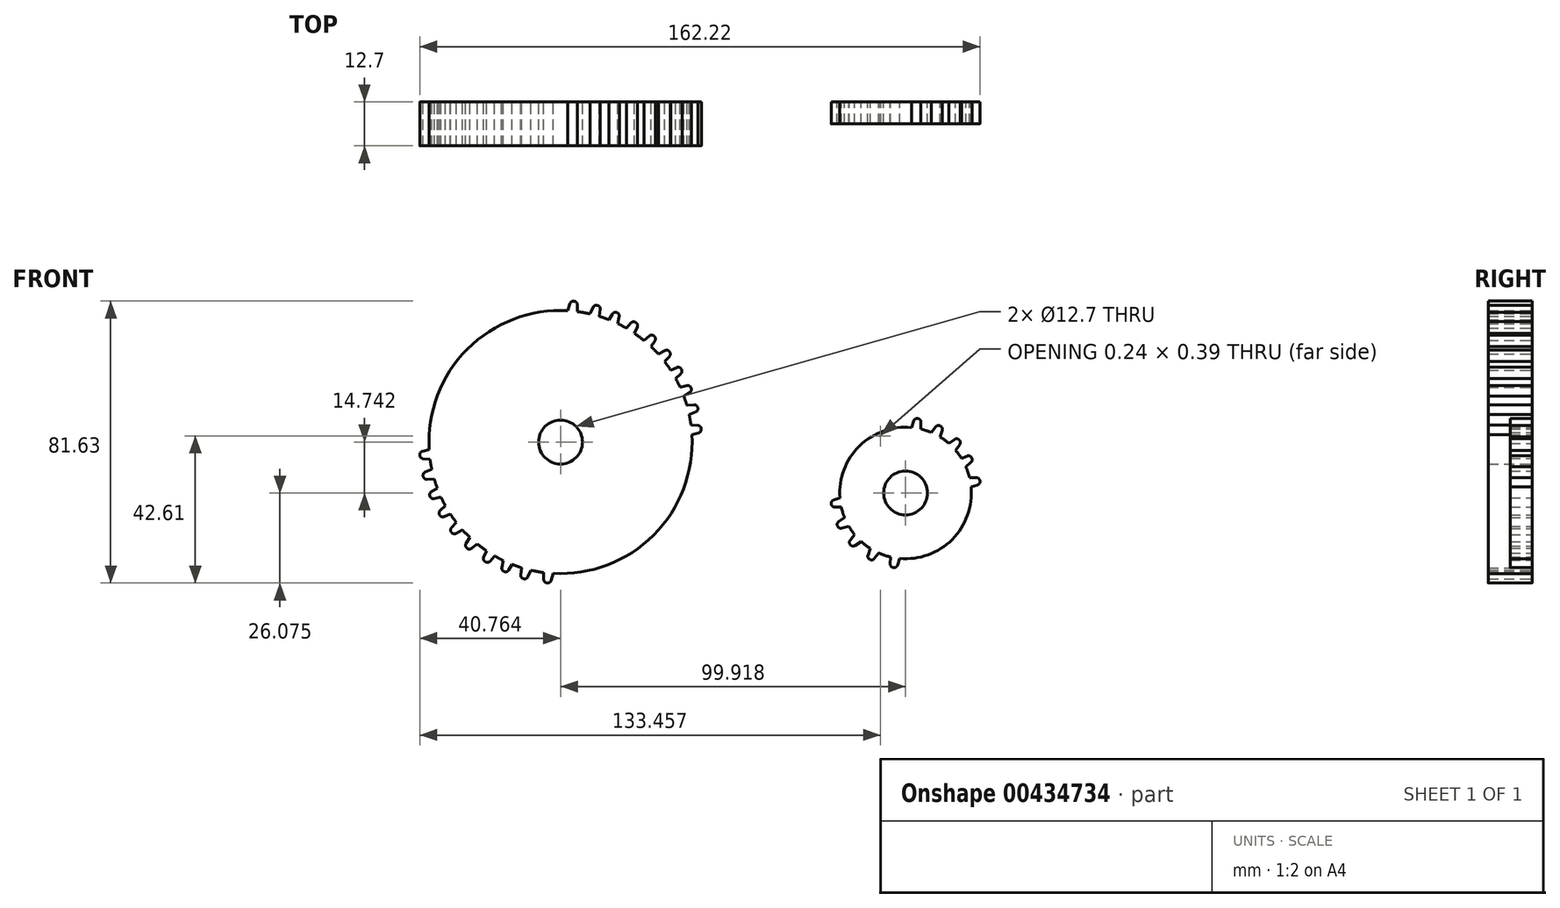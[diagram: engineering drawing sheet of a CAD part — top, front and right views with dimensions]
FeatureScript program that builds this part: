
annotation { "Feature Type Name" : "Feature", "Feature Type Description" : "" }
export const myFeature = defineFeature(function(context is Context, id is Id, definition is map)
    precondition{}
    {
        {
            var Q0;
            Q0=qCreatedBy(makeId("Front.planeOp"),FACE);
            var sketch = newSketch(context, id + "F0", { "sketchPlane" : qUnion([Q0])});
            skCircle(sketch, "E0", {"center": v(-101.86, 31.62) * mm, "radius": 38.1 * mm});
            skCircle(sketch, "E1", {"center": v(-1.94, 16.87) * mm, "radius": 19.05 * mm});
            skCircle(sketch, "E2", {"center": v(-101.86, 31.62) * mm, "radius": 6.35 * mm});
            skCircle(sketch, "E3", {"center": v(-1.94, 16.87) * mm, "radius": 6.35 * mm});
            skCircle(sketch, "E4", {"center": v(-101.86, 31.62) * mm, "radius": 36.92 * mm});
            skCircle(sketch, "E5", {"center": v(-1.94, 16.87) * mm, "radius": 17.88 * mm});
            skPoint(sketch, "E6.visualSharp", {"position": v(-61.92, 41.65) * mm});
            skLineSegment(sketch, "E7", {"start": v(-19.9, 16.87) * mm, "end": v(15.94, 16.87) * mm, "construction": true});
            skLineSegment(sketch, "E8", {"start": v(19.58, 20.42) * mm, "end": v(19.6, 20.3) * mm});
            skLineSegment(sketch, "E9", {"start": v(18.89, 19.18) * mm, "end": v(16.46, 18.44) * mm});
            skLineSegment(sketch, "E10", {"start": v(18.6, 21.3) * mm, "end": v(16.05, 21.36) * mm});
            skLineSegment(sketch, "E11", {"start": v(15.54, 20.78) * mm, "end": v(15.8, 18.85) * mm});
            skPoint(sketch, "E12.visualSharp", {"position": v(19.71, 19.44) * mm});
            skArc(sketch, "E12.filletArc", {"start": v(18.89, 19.18) * mm, "mid": v(19.44, 19.6) * mm, "end": v(19.6, 20.3) * mm});
            skPoint(sketch, "E13.visualSharp", {"position": v(19.46, 21.27) * mm});
            skArc(sketch, "E13.filletArc", {"start": v(19.58, 20.42) * mm, "mid": v(19.25, 21.04) * mm, "end": v(18.6, 21.3) * mm});
            skPoint(sketch, "E14.visualSharp", {"position": v(15.89, 18.26) * mm});
            skArc(sketch, "E14.filletArc", {"start": v(15.8, 18.85) * mm, "mid": v(16.04, 18.5) * mm, "end": v(16.46, 18.44) * mm});
            skPoint(sketch, "E15.visualSharp", {"position": v(14.72, 23.21) * mm});
            skArc(sketch, "E15.filletArc", {"start": v(16.05, 21.36) * mm, "mid": v(15.66, 21.19) * mm, "end": v(15.54, 20.78) * mm});
            skLineSegment(sketch, "E16.0", {"start": v(15.46, 21.37) * mm, "end": v(15.89, 18.26) * mm, "construction": true});
            skLineSegment(sketch, "E17", {"start": v(-1.94, 34.75) * mm, "end": v(-1.94, -1) * mm, "construction": true});
            skLineSegment(sketch, "E18", {"start": v(1.56, 38.42) * mm, "end": v(1.69, 38.4) * mm});
            skLineSegment(sketch, "E19", {"start": v(2.53, 37.38) * mm, "end": v(2.48, 34.75) * mm});
            skLineSegment(sketch, "E20", {"start": v(0.43, 37.76) * mm, "end": v(-0.44, 35.27) * mm});
            skLineSegment(sketch, "E21", {"start": v(0.22, 34.56) * mm, "end": v(2.13, 34.14) * mm});
            skPoint(sketch, "E22.visualSharp", {"position": v(2.55, 38.25) * mm});
            skArc(sketch, "E22.filletArc", {"start": v(2.53, 37.38) * mm, "mid": v(2.3, 38.05) * mm, "end": v(1.69, 38.4) * mm});
            skPoint(sketch, "E23.visualSharp", {"position": v(0.71, 38.57) * mm});
            skArc(sketch, "E23.filletArc", {"start": v(1.56, 38.42) * mm, "mid": v(0.87, 38.3) * mm, "end": v(0.43, 37.76) * mm});
            skPoint(sketch, "E24.visualSharp", {"position": v(2.47, 34.16) * mm});
            skArc(sketch, "E24.filletArc", {"start": v(1.89, 34.26) * mm, "mid": v(2.3, 34.37) * mm, "end": v(2.48, 34.75) * mm});
            skPoint(sketch, "E25.visualSharp", {"position": v(-0.37, 34.68) * mm});
            skArc(sketch, "E25.filletArc", {"start": v(-0.44, 35.27) * mm, "mid": v(-0.4, 34.85) * mm, "end": v(-0.04, 34.6) * mm});
            skLineSegment(sketch, "E26.0", {"start": v(-0.63, 34.7) * mm, "end": v(2.47, 34.16) * mm, "construction": true});
            skLineSegment(sketch, "E27", {"start": v(8.06, 36.3) * mm, "end": v(8.18, 36.25) * mm});
            skLineSegment(sketch, "E28", {"start": v(8.68, 35.03) * mm, "end": v(7.86, 32.53) * mm});
            skLineSegment(sketch, "E29", {"start": v(6.78, 36) * mm, "end": v(5.21, 33.9) * mm});
            skLineSegment(sketch, "E30", {"start": v(5.39, 33.14) * mm, "end": v(7.14, 32.23) * mm});
            skPoint(sketch, "E31.visualSharp", {"position": v(8.94, 35.85) * mm});
            skArc(sketch, "E31.filletArc", {"start": v(8.68, 35.03) * mm, "mid": v(8.65, 35.73) * mm, "end": v(8.18, 36.25) * mm});
            skPoint(sketch, "E32.visualSharp", {"position": v(7.3, 36.7) * mm});
            skArc(sketch, "E32.filletArc", {"start": v(8.06, 36.3) * mm, "mid": v(7.37, 36.4) * mm, "end": v(6.78, 36) * mm});
            skPoint(sketch, "E33.visualSharp", {"position": v(7.67, 31.96) * mm});
            skArc(sketch, "E33.filletArc", {"start": v(7.14, 32.23) * mm, "mid": v(7.57, 32.21) * mm, "end": v(7.86, 32.53) * mm});
            skPoint(sketch, "E34.visualSharp", {"position": v(4.86, 33.41) * mm});
            skArc(sketch, "E34.filletArc", {"start": v(5.21, 33.9) * mm, "mid": v(5.12, 33.48) * mm, "end": v(5.39, 33.14) * mm});
            skLineSegment(sketch, "E35", {"start": v(13.54, 32.27) * mm, "end": v(13.63, 32.18) * mm});
            skLineSegment(sketch, "E36", {"start": v(13.74, 30.87) * mm, "end": v(12.2, 28.73) * mm});
            skLineSegment(sketch, "E37", {"start": v(12.23, 32.38) * mm, "end": v(10.1, 30.84) * mm});
            skLineSegment(sketch, "E38", {"start": v(10.04, 30.07) * mm, "end": v(11.43, 28.67) * mm});
            skPoint(sketch, "E39.visualSharp", {"position": v(14.25, 31.57) * mm});
            skArc(sketch, "E39.filletArc", {"start": v(13.74, 30.87) * mm, "mid": v(13.93, 31.55) * mm, "end": v(13.63, 32.18) * mm});
            skPoint(sketch, "E40.visualSharp", {"position": v(12.93, 32.88) * mm});
            skArc(sketch, "E40.filletArc", {"start": v(13.54, 32.27) * mm, "mid": v(12.9, 32.57) * mm, "end": v(12.23, 32.38) * mm});
            skPoint(sketch, "E41.visualSharp", {"position": v(11.86, 28.25) * mm});
            skArc(sketch, "E41.filletArc", {"start": v(11.43, 28.67) * mm, "mid": v(11.83, 28.52) * mm, "end": v(12.2, 28.73) * mm});
            skPoint(sketch, "E42.visualSharp", {"position": v(9.61, 30.49) * mm});
            skArc(sketch, "E42.filletArc", {"start": v(10.1, 30.84) * mm, "mid": v(9.89, 30.47) * mm, "end": v(10.04, 30.07) * mm});
            skLineSegment(sketch, "E43.0", {"start": v(9.61, 30.49) * mm, "end": v(11.86, 28.25) * mm, "construction": true});
            skLineSegment(sketch, "E44", {"start": v(17.15, 27.13) * mm, "end": v(17.21, 27.02) * mm});
            skLineSegment(sketch, "E45", {"start": v(16.98, 25.73) * mm, "end": v(14.96, 24.05) * mm});
            skLineSegment(sketch, "E46", {"start": v(15.9, 27.57) * mm, "end": v(13.45, 26.62) * mm});
            skLineSegment(sketch, "E47", {"start": v(13.2, 25.89) * mm, "end": v(14.2, 24.18) * mm});
            skPoint(sketch, "E48.visualSharp", {"position": v(17.65, 26.28) * mm});
            skArc(sketch, "E48.filletArc", {"start": v(16.98, 25.73) * mm, "mid": v(17.34, 26.33) * mm, "end": v(17.21, 27.02) * mm});
            skPoint(sketch, "E49.visualSharp", {"position": v(16.71, 27.88) * mm});
            skArc(sketch, "E49.filletArc", {"start": v(17.15, 27.13) * mm, "mid": v(16.6, 27.58) * mm, "end": v(15.9, 27.57) * mm});
            skPoint(sketch, "E50.visualSharp", {"position": v(15.3, 21.85) * mm});
            skArc(sketch, "E50.filletArc", {"start": v(14.2, 24.18) * mm, "mid": v(14.54, 23.94) * mm, "end": v(14.96, 24.05) * mm});
            skPoint(sketch, "E51.visualSharp", {"position": v(11.92, 28.33) * mm});
            skArc(sketch, "E51.filletArc", {"start": v(13.45, 26.62) * mm, "mid": v(13.15, 26.31) * mm, "end": v(13.2, 25.89) * mm});
            skLineSegment(sketch, "E52.0", {"start": v(13.92, 25.13) * mm, "end": v(15.15, 22.2) * mm, "construction": true});
            skCircle(sketch, "E53.MirrorC", {"center": v(-1.94, 16.87) * mm, "radius": 17.88 * mm, "construction": true});
            skPoint(sketch, "E54.MirrorP", {"position": v(-6.83, 38.1) * mm});
            skArc(sketch, "E55.MirrorCS", {"start": v(-6.78, 37.23) * mm, "mid": v(-6.58, 37.9) * mm, "end": v(-5.98, 38.28) * mm});
            skArc(sketch, "E56.MirrorCS", {"start": v(-5.86, 38.3) * mm, "mid": v(-5.17, 38.21) * mm, "end": v(-4.7, 37.69) * mm});
            skLineSegment(sketch, "E57.MirrorCS", {"start": v(-4.7, 37.69) * mm, "end": v(-3.58, 34.86) * mm});
            skLineSegment(sketch, "E58.MirrorCS", {"start": v(-6.78, 37.23) * mm, "end": v(-6.63, 34.6) * mm});
            skArc(sketch, "E59.MirrorCS", {"start": v(-6.01, 34.14) * mm, "mid": v(-6.43, 34.23) * mm, "end": v(-6.63, 34.6) * mm});
            skArc(sketch, "E60.MirrorCS", {"start": v(-3.73, 35.24) * mm, "mid": v(-3.76, 34.81) * mm, "end": v(-4.1, 34.56) * mm});
            skLineSegment(sketch, "E61.MirrorCS", {"start": v(-3.51, 34.68) * mm, "end": v(-6.6, 34.01) * mm, "construction": true});
            skLineSegment(sketch, "E62.MirrorCS", {"start": v(-10.85, 35.72) * mm, "end": v(-9.04, 33.27) * mm});
            skArc(sketch, "E63.MirrorCS", {"start": v(-12.13, 36.02) * mm, "mid": v(-11.44, 36.1) * mm, "end": v(-10.85, 35.72) * mm});
            skArc(sketch, "E64.MirrorCS", {"start": v(-12.75, 34.74) * mm, "mid": v(-12.72, 35.44) * mm, "end": v(-12.25, 35.96) * mm});
            skLineSegment(sketch, "E65.MirrorCS", {"start": v(-12.75, 34.74) * mm, "end": v(-11.93, 32.24) * mm});
            skArc(sketch, "E66.MirrorCS", {"start": v(-9.28, 33.6) * mm, "mid": v(-9.2, 33.19) * mm, "end": v(-9.46, 32.85) * mm});
            skArc(sketch, "E67.MirrorCS", {"start": v(-11.21, 31.94) * mm, "mid": v(-11.64, 31.92) * mm, "end": v(-11.93, 32.24) * mm});
            skLineSegment(sketch, "E68.MirrorCS", {"start": v(-8.93, 33.12) * mm, "end": v(-11.74, 31.67) * mm, "construction": true});
            skLineSegment(sketch, "E69.MirrorCS", {"start": v(-16.24, 32.23) * mm, "end": v(-14.04, 30.78) * mm});
            skArc(sketch, "E70.MirrorCS", {"start": v(-17.54, 32.07) * mm, "mid": v(-16.92, 32.4) * mm, "end": v(-16.24, 32.23) * mm});
            skArc(sketch, "E71.MirrorCS", {"start": v(-17.68, 30.67) * mm, "mid": v(-17.9, 31.33) * mm, "end": v(-17.63, 31.98) * mm});
            skLineSegment(sketch, "E72.MirrorCS", {"start": v(-17.68, 30.67) * mm, "end": v(-16.06, 28.6) * mm});
            skArc(sketch, "E73.MirrorCS", {"start": v(-14.04, 30.78) * mm, "mid": v(-13.81, 30.42) * mm, "end": v(-13.95, 30.01) * mm});
            skArc(sketch, "E74.MirrorCS", {"start": v(-15.28, 28.56) * mm, "mid": v(-15.68, 28.4) * mm, "end": v(-16.06, 28.6) * mm});
            skLineSegment(sketch, "E75.MirrorCS", {"start": v(-13.54, 30.45) * mm, "end": v(-15.69, 28.12) * mm, "construction": true});
            skLineSegment(sketch, "E76.MirrorCS", {"start": v(-20.35, 26.86) * mm, "end": v(-17.8, 26.25) * mm});
            skArc(sketch, "E77.MirrorCS", {"start": v(-21.53, 26.26) * mm, "mid": v(-21.05, 26.77) * mm, "end": v(-20.35, 26.86) * mm});
            skArc(sketch, "E78.MirrorCS", {"start": v(-21.18, 24.89) * mm, "mid": v(-21.6, 25.44) * mm, "end": v(-21.58, 26.14) * mm});
            skLineSegment(sketch, "E79.MirrorCS", {"start": v(-21.18, 24.89) * mm, "end": v(-18.94, 23.5) * mm});
            skArc(sketch, "E80.MirrorCS", {"start": v(-18.2, 23.73) * mm, "mid": v(-18.52, 23.44) * mm, "end": v(-18.94, 23.5) * mm});
            skArc(sketch, "E81.MirrorCS", {"start": v(-17.8, 26.25) * mm, "mid": v(-17.46, 25.98) * mm, "end": v(-17.44, 25.55) * mm});
            skLineSegment(sketch, "E82.MirrorCS", {"start": v(-22.55, 21.03) * mm, "end": v(-20, 21.1) * mm});
            skArc(sketch, "E83.MirrorCS", {"start": v(-23.52, 20.14) * mm, "mid": v(-23.2, 20.76) * mm, "end": v(-22.55, 21.03) * mm});
            skArc(sketch, "E84.MirrorCS", {"start": v(-22.82, 18.91) * mm, "mid": v(-23.38, 19.33) * mm, "end": v(-23.54, 20.02) * mm});
            skLineSegment(sketch, "E85.MirrorCS", {"start": v(-22.82, 18.91) * mm, "end": v(-20.4, 18.18) * mm});
            skLineSegment(sketch, "E86.MirrorCS", {"start": v(-19.41, 21.13) * mm, "end": v(-19.82, 18.01) * mm, "construction": true});
            skArc(sketch, "E87.MirrorCS", {"start": v(-20, 21.1) * mm, "mid": v(-19.62, 20.94) * mm, "end": v(-19.49, 20.53) * mm});
            skArc(sketch, "E88.MirrorCS", {"start": v(-19.74, 18.6) * mm, "mid": v(-19.97, 18.24) * mm, "end": v(-20.4, 18.18) * mm});
            skLineSegment(sketch, "E89.MirrorCS", {"start": v(0.44, -3.97) * mm, "end": v(-0.3, -1.45) * mm});
            skArc(sketch, "E90.MirrorCS", {"start": v(1.55, -4.7) * mm, "mid": v(0.86, -4.53) * mm, "end": v(0.44, -3.97) * mm});
            skArc(sketch, "E91.MirrorCS", {"start": v(2.56, -3.7) * mm, "mid": v(2.3, -4.35) * mm, "end": v(1.67, -4.67) * mm});
            skLineSegment(sketch, "E92.MirrorCS", {"start": v(2.56, -3.7) * mm, "end": v(2.63, -1.07) * mm});
            skArc(sketch, "E93.MirrorCS", {"start": v(2.06, -0.55) * mm, "mid": v(2.47, -0.68) * mm, "end": v(2.63, -1.07) * mm});
            skArc(sketch, "E94.MirrorCS", {"start": v(-0.3, -1.45) * mm, "mid": v(-0.25, -1.03) * mm, "end": v(0.12, -0.8) * mm});
            skLineSegment(sketch, "E95.MirrorCS", {"start": v(-0.48, -0.88) * mm, "end": v(2.65, -0.47) * mm, "construction": true});
            skArc(sketch, "E96.MirrorCS", {"start": v(8.1, -2.6) * mm, "mid": v(7.41, -2.7) * mm, "end": v(6.83, -2.31) * mm});
            skArc(sketch, "E97.MirrorCS", {"start": v(8.72, -1.33) * mm, "mid": v(8.7, -2.03) * mm, "end": v(8.22, -2.55) * mm});
            skLineSegment(sketch, "E98.MirrorCS", {"start": v(8.72, -1.33) * mm, "end": v(7.9, 1.17) * mm});
            skLineSegment(sketch, "E99.MirrorCS", {"start": v(6.83, -2.31) * mm, "end": v(5.26, -0.2) * mm});
            skArc(sketch, "E100.MirrorCS", {"start": v(5.26, -0.2) * mm, "mid": v(5.17, 0.22) * mm, "end": v(5.43, 0.56) * mm});
            skArc(sketch, "E101.MirrorCS", {"start": v(7.19, 1.46) * mm, "mid": v(7.61, 1.48) * mm, "end": v(7.9, 1.17) * mm});
            skLineSegment(sketch, "E102.MirrorCS", {"start": v(4.9, 0.28) * mm, "end": v(7.72, 1.74) * mm, "construction": true});
            skArc(sketch, "E103.MirrorCS", {"start": v(13.67, 1.66) * mm, "mid": v(13.04, 1.36) * mm, "end": v(12.36, 1.55) * mm});
            skLineSegment(sketch, "E104.MirrorCS", {"start": v(12.36, 1.55) * mm, "end": v(10.22, 3.09) * mm});
            skArc(sketch, "E105.MirrorCS", {"start": v(10.22, 3.09) * mm, "mid": v(10.01, 3.46) * mm, "end": v(10.16, 3.86) * mm});
            skLineSegment(sketch, "E106.MirrorCS", {"start": v(9.74, 3.43) * mm, "end": v(11.98, 5.68) * mm, "construction": true});
            skArc(sketch, "E107.MirrorCS", {"start": v(11.55, 5.26) * mm, "mid": v(11.95, 5.4) * mm, "end": v(12.33, 5.2) * mm});
            skLineSegment(sketch, "E108.MirrorCS", {"start": v(13.87, 3.06) * mm, "end": v(12.33, 5.2) * mm});
            skArc(sketch, "E109.MirrorCS", {"start": v(13.87, 3.06) * mm, "mid": v(14.06, 2.39) * mm, "end": v(13.76, 1.75) * mm});
            skLineSegment(sketch, "E110.MirrorCS", {"start": v(18.55, 12.8) * mm, "end": v(16.01, 12.63) * mm});
            skArc(sketch, "E111.MirrorCS", {"start": v(19.49, 13.73) * mm, "mid": v(19.19, 13.1) * mm, "end": v(18.55, 12.8) * mm});
            skArc(sketch, "E112.MirrorCS", {"start": v(18.74, 14.93) * mm, "mid": v(19.32, 14.53) * mm, "end": v(19.5, 13.85) * mm});
            skLineSegment(sketch, "E113.MirrorCS", {"start": v(18.74, 14.93) * mm, "end": v(16.29, 15.57) * mm});
            skArc(sketch, "E114.MirrorCS", {"start": v(15.65, 15.12) * mm, "mid": v(15.87, 15.5) * mm, "end": v(16.29, 15.57) * mm});
            skLineSegment(sketch, "E115.MirrorCS", {"start": v(15.42, 12.59) * mm, "end": v(15.7, 15.72) * mm, "construction": true});
            skArc(sketch, "E116.MirrorCS", {"start": v(16.01, 12.63) * mm, "mid": v(15.62, 12.78) * mm, "end": v(15.47, 13.18) * mm});
            skArc(sketch, "E117.MirrorCS", {"start": v(-5.41, -4.75) * mm, "mid": v(-4.73, -4.62) * mm, "end": v(-4.28, -4.07) * mm});
            skLineSegment(sketch, "E118.MirrorCS", {"start": v(-4.28, -4.07) * mm, "end": v(-3.43, -1.58) * mm});
            skArc(sketch, "E119.MirrorCS", {"start": v(-3.43, -1.58) * mm, "mid": v(-3.47, -1.16) * mm, "end": v(-3.82, -0.92) * mm});
            skLineSegment(sketch, "E120.MirrorCS", {"start": v(-3.23, -1.02) * mm, "end": v(-6.34, -0.49) * mm, "construction": true});
            skArc(sketch, "E121.MirrorCS", {"start": v(-5.76, -0.59) * mm, "mid": v(-6.17, -0.7) * mm, "end": v(-6.35, -1.08) * mm});
            skLineSegment(sketch, "E122.MirrorCS", {"start": v(-6.38, -3.7) * mm, "end": v(-6.35, -1.08) * mm});
            skArc(sketch, "E123.MirrorCS", {"start": v(-12.23, -2.4) * mm, "mid": v(-11.53, -2.5) * mm, "end": v(-10.94, -2.11) * mm});
            skArc(sketch, "E124.MirrorCS", {"start": v(-12.83, -1.13) * mm, "mid": v(-12.81, -1.83) * mm, "end": v(-12.34, -2.35) * mm});
            skLineSegment(sketch, "E125.MirrorCS", {"start": v(-12.83, -1.13) * mm, "end": v(-12, 1.37) * mm});
            skLineSegment(sketch, "E126.MirrorCS", {"start": v(-10.94, -2.11) * mm, "end": v(-9.37, 0) * mm});
            skArc(sketch, "E127.MirrorCS", {"start": v(-9.37, 0) * mm, "mid": v(-9.28, 0.41) * mm, "end": v(-9.54, 0.75) * mm});
            skLineSegment(sketch, "E128.MirrorCS", {"start": v(-9, 0.47) * mm, "end": v(-11.82, 1.94) * mm, "construction": true});
            skArc(sketch, "E129.MirrorCS", {"start": v(-11.29, 1.66) * mm, "mid": v(-11.71, 1.69) * mm, "end": v(-12, 1.37) * mm});
            skLineSegment(sketch, "E130.MirrorCS", {"start": v(-16.53, 1.62) * mm, "end": v(-14.34, 3.07) * mm});
            skArc(sketch, "E131.MirrorCS", {"start": v(-17.84, 1.78) * mm, "mid": v(-17.22, 1.46) * mm, "end": v(-16.53, 1.62) * mm});
            skArc(sketch, "E132.MirrorCS", {"start": v(-17.98, 3.19) * mm, "mid": v(-18.2, 2.52) * mm, "end": v(-17.93, 1.87) * mm});
            skLineSegment(sketch, "E133.MirrorCS", {"start": v(-17.98, 3.19) * mm, "end": v(-16.35, 5.26) * mm});
            skArc(sketch, "E134.MirrorCS", {"start": v(-15.58, 5.29) * mm, "mid": v(-15.97, 5.45) * mm, "end": v(-16.35, 5.26) * mm});
            skLineSegment(sketch, "E135.MirrorCS", {"start": v(-13.84, 3.4) * mm, "end": v(-15.98, 5.73) * mm, "construction": true});
            skArc(sketch, "E136.MirrorCS", {"start": v(-14.34, 3.07) * mm, "mid": v(-14.11, 3.43) * mm, "end": v(-14.24, 3.84) * mm});
            skLineSegment(sketch, "E137.MirrorCS", {"start": v(-20.4, 6.66) * mm, "end": v(-17.87, 7.38) * mm});
            skArc(sketch, "E138.MirrorCS", {"start": v(-21.6, 7.21) * mm, "mid": v(-21.1, 6.72) * mm, "end": v(-20.4, 6.66) * mm});
            skArc(sketch, "E139.MirrorCS", {"start": v(-21.3, 8.6) * mm, "mid": v(-21.71, 8.03) * mm, "end": v(-21.65, 7.33) * mm});
            skLineSegment(sketch, "E140.MirrorCS", {"start": v(-21.3, 8.6) * mm, "end": v(-19.13, 10.08) * mm});
            skArc(sketch, "E141.MirrorCS", {"start": v(-18.38, 9.87) * mm, "mid": v(-18.7, 10.15) * mm, "end": v(-19.13, 10.08) * mm});
            skArc(sketch, "E142.MirrorCS", {"start": v(-17.87, 7.38) * mm, "mid": v(-17.54, 7.65) * mm, "end": v(-17.55, 8.08) * mm});
            skLineSegment(sketch, "E143.MirrorCS", {"start": v(-22.43, 12.77) * mm, "end": v(-19.89, 12.77) * mm});
            skArc(sketch, "E144.MirrorCS", {"start": v(-23.43, 13.62) * mm, "mid": v(-23.09, 13) * mm, "end": v(-22.43, 12.77) * mm});
            skArc(sketch, "E145.MirrorCS", {"start": v(-22.78, 14.87) * mm, "mid": v(-23.32, 14.43) * mm, "end": v(-23.45, 13.74) * mm});
            skLineSegment(sketch, "E146.MirrorCS", {"start": v(-22.78, 14.87) * mm, "end": v(-20.37, 15.68) * mm});
            skLineSegment(sketch, "E147.MirrorCS", {"start": v(-19.29, 12.78) * mm, "end": v(-19.8, 15.88) * mm, "construction": true});
            skArc(sketch, "E148.MirrorCS", {"start": v(-19.7, 15.29) * mm, "mid": v(-19.95, 15.64) * mm, "end": v(-20.37, 15.68) * mm});
            skArc(sketch, "E149.MirrorCS", {"start": v(-19.89, 12.77) * mm, "mid": v(-19.5, 12.95) * mm, "end": v(-19.39, 13.37) * mm});
            skLineSegment(sketch, "E150", {"start": v(-5.98, 38.28) * mm, "end": v(-5.86, 38.3) * mm});
            skLineSegment(sketch, "E151", {"start": v(-12.25, 35.96) * mm, "end": v(-12.13, 36.02) * mm});
            skLineSegment(sketch, "E152", {"start": v(-17.63, 31.98) * mm, "end": v(-17.54, 32.07) * mm});
            skLineSegment(sketch, "E153", {"start": v(-21.58, 26.14) * mm, "end": v(-21.53, 26.26) * mm});
            skLineSegment(sketch, "E154", {"start": v(-23.54, 20.02) * mm, "end": v(-23.52, 20.14) * mm});
            skLineSegment(sketch, "E155", {"start": v(-23.43, 13.62) * mm, "end": v(-23.45, 13.74) * mm});
            skLineSegment(sketch, "E156", {"start": v(-21.6, 7.21) * mm, "end": v(-21.65, 7.33) * mm});
            skLineSegment(sketch, "E157", {"start": v(-17.84, 1.78) * mm, "end": v(-17.93, 1.87) * mm});
            skLineSegment(sketch, "E158", {"start": v(-12.23, -2.4) * mm, "end": v(-12.34, -2.35) * mm});
            skLineSegment(sketch, "E159", {"start": v(1.67, -4.67) * mm, "end": v(1.55, -4.7) * mm});
            skLineSegment(sketch, "E160", {"start": v(8.22, -2.55) * mm, "end": v(8.1, -2.6) * mm});
            skLineSegment(sketch, "E161", {"start": v(13.76, 1.75) * mm, "end": v(13.67, 1.66) * mm});
            skLineSegment(sketch, "E162", {"start": v(19.5, 13.85) * mm, "end": v(19.49, 13.73) * mm});
            skArc(sketch, "E163.MirrorCS", {"start": v(-6.38, -3.7) * mm, "mid": v(-6.15, -4.37) * mm, "end": v(-5.54, -4.72) * mm});
            skLineSegment(sketch, "E164.MirrorCS", {"start": v(-5.54, -4.72) * mm, "end": v(-5.41, -4.75) * mm});
            skLineSegment(sketch, "E165.MirrorCS", {"start": v(17.43, 8.5) * mm, "end": v(15.33, 10.08) * mm});
            skArc(sketch, "E166.MirrorCS", {"start": v(14.57, 9.9) * mm, "mid": v(14.9, 10.17) * mm, "end": v(15.33, 10.08) * mm});
            skArc(sketch, "E167.MirrorCS", {"start": v(13.94, 7.44) * mm, "mid": v(13.63, 7.73) * mm, "end": v(13.65, 8.16) * mm});
            skLineSegment(sketch, "E168.MirrorCS", {"start": v(16.44, 6.6) * mm, "end": v(13.94, 7.44) * mm});
            skArc(sketch, "E169.MirrorCS", {"start": v(17.66, 7.1) * mm, "mid": v(17.14, 6.63) * mm, "end": v(16.44, 6.6) * mm});
            skArc(sketch, "E170.MirrorCS", {"start": v(17.43, 8.5) * mm, "mid": v(17.8, 7.9) * mm, "end": v(17.72, 7.21) * mm});
            skLineSegment(sketch, "E171.MirrorCS", {"start": v(17.66, 7.1) * mm, "end": v(17.72, 7.21) * mm});
            skLineSegment(sketch, "E172", {"start": v(-101.86, 69.72) * mm, "end": v(-101.86, -6.48) * mm, "construction": true});
            skLineSegment(sketch, "E173", {"start": v(-139.96, 31.62) * mm, "end": v(-63.76, 31.62) * mm, "construction": true});
            skLineSegment(sketch, "E174.MirrorCS", {"start": v(-141.66, 35.84) * mm, "end": v(-139.03, 36.02) * mm});
            skArc(sketch, "E175.MirrorCS", {"start": v(-142.6, 34.92) * mm, "mid": v(-142.3, 35.56) * mm, "end": v(-141.66, 35.84) * mm});
            skArc(sketch, "E176.MirrorCS", {"start": v(-141.86, 33.72) * mm, "mid": v(-142.43, 34.12) * mm, "end": v(-142.61, 34.8) * mm});
            skLineSegment(sketch, "E177.MirrorCS", {"start": v(-141.86, 33.72) * mm, "end": v(-139.31, 33.05) * mm});
            skArc(sketch, "E178.MirrorCS", {"start": v(-139.03, 36.02) * mm, "mid": v(-138.63, 35.87) * mm, "end": v(-138.5, 35.46) * mm});
            skArc(sketch, "E179.MirrorCS", {"start": v(-138.68, 33.5) * mm, "mid": v(-138.9, 33.13) * mm, "end": v(-139.31, 33.05) * mm});
            skLineSegment(sketch, "E180.MirrorCS", {"start": v(-138.43, 36.06) * mm, "end": v(-138.73, 32.9) * mm, "construction": true});
            skLineSegment(sketch, "E181", {"start": v(-142.61, 34.8) * mm, "end": v(-142.6, 34.92) * mm});
            skLineSegment(sketch, "E182.MirrorCS", {"start": v(-140.7, 41.97) * mm, "end": v(-138.07, 41.8) * mm});
            skArc(sketch, "E183.MirrorCS", {"start": v(-141.75, 41.17) * mm, "mid": v(-141.36, 41.76) * mm, "end": v(-140.7, 41.97) * mm});
            skArc(sketch, "E184.MirrorCS", {"start": v(-141.16, 39.89) * mm, "mid": v(-141.68, 40.36) * mm, "end": v(-141.77, 41.05) * mm});
            skLineSegment(sketch, "E185.MirrorCS", {"start": v(-141.16, 39.89) * mm, "end": v(-138.72, 38.9) * mm});
            skArc(sketch, "E186.MirrorCS", {"start": v(-138.07, 41.8) * mm, "mid": v(-137.69, 41.6) * mm, "end": v(-137.6, 41.19) * mm});
            skArc(sketch, "E187.MirrorCS", {"start": v(-138.03, 39.26) * mm, "mid": v(-138.3, 38.92) * mm, "end": v(-138.72, 38.9) * mm});
            skLineSegment(sketch, "E188.MirrorCS", {"start": v(-137.47, 41.77) * mm, "end": v(-138.16, 38.68) * mm, "construction": true});
            skLineSegment(sketch, "E189", {"start": v(-141.77, 41.05) * mm, "end": v(-141.75, 41.17) * mm});
            skLineSegment(sketch, "E190.MirrorCS", {"start": v(-138.45, 47.99) * mm, "end": v(-135.89, 47.37) * mm});
            skArc(sketch, "E191.MirrorCS", {"start": v(-139.62, 47.39) * mm, "mid": v(-139.15, 47.9) * mm, "end": v(-138.45, 47.99) * mm});
            skArc(sketch, "E192.MirrorCS", {"start": v(-139.27, 46.02) * mm, "mid": v(-139.7, 46.57) * mm, "end": v(-139.67, 47.27) * mm});
            skLineSegment(sketch, "E193.MirrorCS", {"start": v(-139.27, 46.02) * mm, "end": v(-137.04, 44.63) * mm});
            skArc(sketch, "E194.MirrorCS", {"start": v(-135.89, 47.37) * mm, "mid": v(-135.55, 47.1) * mm, "end": v(-135.54, 46.68) * mm});
            skArc(sketch, "E195.MirrorCS", {"start": v(-136.3, 44.86) * mm, "mid": v(-136.61, 44.57) * mm, "end": v(-137.04, 44.63) * mm});
            skLineSegment(sketch, "E196.MirrorCS", {"start": v(-135.3, 47.23) * mm, "end": v(-136.53, 44.3) * mm, "construction": true});
            skLineSegment(sketch, "E197", {"start": v(-139.67, 47.27) * mm, "end": v(-139.62, 47.39) * mm});
            skLineSegment(sketch, "E198.MirrorCS", {"start": v(-104, 71.78) * mm, "end": v(-103.26, 69.26) * mm});
            skArc(sketch, "E199.MirrorCS", {"start": v(-105.1, 72.5) * mm, "mid": v(-104.43, 72.34) * mm, "end": v(-104, 71.78) * mm});
            skArc(sketch, "E200.MirrorCS", {"start": v(-106.12, 71.51) * mm, "mid": v(-105.86, 72.16) * mm, "end": v(-105.24, 72.48) * mm});
            skLineSegment(sketch, "E201.MirrorCS", {"start": v(-106.12, 71.51) * mm, "end": v(-106.21, 68.88) * mm});
            skArc(sketch, "E202.MirrorCS", {"start": v(-103.26, 69.26) * mm, "mid": v(-103.32, 68.84) * mm, "end": v(-103.68, 68.6) * mm});
            skArc(sketch, "E203.MirrorCS", {"start": v(-105.64, 68.36) * mm, "mid": v(-106.04, 68.49) * mm, "end": v(-106.21, 68.88) * mm});
            skLineSegment(sketch, "E204.MirrorCS", {"start": v(-103.08, 68.69) * mm, "end": v(-106.23, 68.28) * mm, "construction": true});
            skLineSegment(sketch, "E205", {"start": v(-105.24, 72.48) * mm, "end": v(-105.1, 72.5) * mm});
            skLineSegment(sketch, "E206.MirrorCS", {"start": v(-110.44, 70.7) * mm, "end": v(-109.47, 68.26) * mm});
            skArc(sketch, "E207.MirrorCS", {"start": v(-111.6, 71.32) * mm, "mid": v(-110.9, 71.23) * mm, "end": v(-110.44, 70.7) * mm});
            skArc(sketch, "E208.MirrorCS", {"start": v(-112.52, 70.25) * mm, "mid": v(-112.31, 70.92) * mm, "end": v(-111.72, 71.3) * mm});
            skLineSegment(sketch, "E209.MirrorCS", {"start": v(-112.52, 70.25) * mm, "end": v(-112.38, 67.62) * mm});
            skArc(sketch, "E210.MirrorCS", {"start": v(-109.47, 68.26) * mm, "mid": v(-109.5, 67.83) * mm, "end": v(-109.83, 67.57) * mm});
            skArc(sketch, "E211.MirrorCS", {"start": v(-111.76, 67.15) * mm, "mid": v(-112.18, 67.24) * mm, "end": v(-112.38, 67.62) * mm});
            skLineSegment(sketch, "E212.MirrorCS", {"start": v(-109.25, 67.7) * mm, "end": v(-112.35, 67.02) * mm, "construction": true});
            skLineSegment(sketch, "E213", {"start": v(-111.72, 71.3) * mm, "end": v(-111.6, 71.32) * mm});
            skLineSegment(sketch, "E214.MirrorCS", {"start": v(-116.88, 68.72) * mm, "end": v(-115.5, 66.48) * mm});
            skArc(sketch, "E215.MirrorCS", {"start": v(-118.13, 69.13) * mm, "mid": v(-117.43, 69.16) * mm, "end": v(-116.88, 68.72) * mm});
            skArc(sketch, "E216.MirrorCS", {"start": v(-118.86, 67.91) * mm, "mid": v(-118.77, 68.6) * mm, "end": v(-118.25, 69.08) * mm});
            skLineSegment(sketch, "E217.MirrorCS", {"start": v(-118.86, 67.91) * mm, "end": v(-118.26, 65.35) * mm});
            skArc(sketch, "E218.MirrorCS", {"start": v(-115.5, 66.48) * mm, "mid": v(-115.45, 66.05) * mm, "end": v(-115.74, 65.74) * mm});
            skArc(sketch, "E219.MirrorCS", {"start": v(-117.57, 65) * mm, "mid": v(-118, 65) * mm, "end": v(-118.26, 65.35) * mm});
            skLineSegment(sketch, "E220.MirrorCS", {"start": v(-115.2, 65.97) * mm, "end": v(-118.13, 64.76) * mm, "construction": true});
            skLineSegment(sketch, "E221", {"start": v(-118.25, 69.08) * mm, "end": v(-118.13, 69.13) * mm});
            skLineSegment(sketch, "E222.MirrorCS", {"start": v(-135.54, 53.22) * mm, "end": v(-133.13, 52.17) * mm});
            skArc(sketch, "E223.MirrorCS", {"start": v(-136.8, 52.83) * mm, "mid": v(-136.24, 53.26) * mm, "end": v(-135.54, 53.22) * mm});
            skArc(sketch, "E224.MirrorCS", {"start": v(-136.7, 51.42) * mm, "mid": v(-137.02, 52.04) * mm, "end": v(-136.87, 52.73) * mm});
            skLineSegment(sketch, "E225.MirrorCS", {"start": v(-136.7, 51.42) * mm, "end": v(-134.74, 49.66) * mm});
            skArc(sketch, "E226.MirrorCS", {"start": v(-133.13, 52.17) * mm, "mid": v(-132.84, 51.85) * mm, "end": v(-132.9, 51.43) * mm});
            skArc(sketch, "E227.MirrorCS", {"start": v(-133.97, 49.77) * mm, "mid": v(-134.33, 49.54) * mm, "end": v(-134.74, 49.66) * mm});
            skLineSegment(sketch, "E228.MirrorCS", {"start": v(-132.58, 51.93) * mm, "end": v(-134.3, 49.26) * mm, "construction": true});
            skLineSegment(sketch, "E229", {"start": v(-136.87, 52.73) * mm, "end": v(-136.8, 52.83) * mm});
            skLineSegment(sketch, "E230.MirrorCS", {"start": v(-122.28, 66.13) * mm, "end": v(-120.54, 64.16) * mm});
            skArc(sketch, "E231.MirrorCS", {"start": v(-123.59, 66.31) * mm, "mid": v(-122.9, 66.46) * mm, "end": v(-122.28, 66.13) * mm});
            skArc(sketch, "E232.MirrorCS", {"start": v(-124.08, 64.99) * mm, "mid": v(-124.12, 65.69) * mm, "end": v(-123.7, 66.24) * mm});
            skLineSegment(sketch, "E233.MirrorCS", {"start": v(-124.08, 64.99) * mm, "end": v(-123.05, 62.56) * mm});
            skArc(sketch, "E234.MirrorCS", {"start": v(-120.54, 64.16) * mm, "mid": v(-120.41, 63.75) * mm, "end": v(-120.64, 63.39) * mm});
            skArc(sketch, "E235.MirrorCS", {"start": v(-122.31, 62.33) * mm, "mid": v(-122.74, 62.28) * mm, "end": v(-123.05, 62.56) * mm});
            skLineSegment(sketch, "E236.MirrorCS", {"start": v(-120.14, 63.7) * mm, "end": v(-122.82, 62.01) * mm, "construction": true});
            skLineSegment(sketch, "E237", {"start": v(-123.7, 66.24) * mm, "end": v(-123.59, 66.31) * mm});
            skLineSegment(sketch, "E238.MirrorCS", {"start": v(-132.08, 58.1) * mm, "end": v(-129.77, 56.85) * mm});
            skArc(sketch, "E239.MirrorCS", {"start": v(-133.37, 57.83) * mm, "mid": v(-132.78, 58.2) * mm, "end": v(-132.08, 58.1) * mm});
            skArc(sketch, "E240.MirrorCS", {"start": v(-133.39, 56.42) * mm, "mid": v(-133.66, 57.06) * mm, "end": v(-133.45, 57.73) * mm});
            skLineSegment(sketch, "E241.MirrorCS", {"start": v(-133.39, 56.42) * mm, "end": v(-131.59, 54.5) * mm});
            skArc(sketch, "E242.MirrorCS", {"start": v(-129.77, 56.85) * mm, "mid": v(-129.51, 56.5) * mm, "end": v(-129.6, 56.1) * mm});
            skArc(sketch, "E243.MirrorCS", {"start": v(-130.81, 54.53) * mm, "mid": v(-131.2, 54.33) * mm, "end": v(-131.59, 54.5) * mm});
            skLineSegment(sketch, "E244.MirrorCS", {"start": v(-129.24, 56.57) * mm, "end": v(-131.18, 54.06) * mm, "construction": true});
            skLineSegment(sketch, "E245", {"start": v(-133.45, 57.73) * mm, "end": v(-133.37, 57.83) * mm});
            skLineSegment(sketch, "E246.MirrorCS", {"start": v(-127.62, 62.4) * mm, "end": v(-125.55, 60.76) * mm});
            skArc(sketch, "E247.MirrorCS", {"start": v(-128.93, 62.35) * mm, "mid": v(-128.28, 62.61) * mm, "end": v(-127.62, 62.4) * mm});
            skArc(sketch, "E248.MirrorCS", {"start": v(-129.2, 60.96) * mm, "mid": v(-129.35, 61.64) * mm, "end": v(-129.03, 62.26) * mm});
            skLineSegment(sketch, "E249.MirrorCS", {"start": v(-129.2, 60.96) * mm, "end": v(-127.76, 58.75) * mm});
            skArc(sketch, "E250.MirrorCS", {"start": v(-125.55, 60.76) * mm, "mid": v(-125.36, 60.38) * mm, "end": v(-125.53, 59.98) * mm});
            skArc(sketch, "E251.MirrorCS", {"start": v(-126.99, 58.65) * mm, "mid": v(-127.4, 58.52) * mm, "end": v(-127.76, 58.75) * mm});
            skLineSegment(sketch, "E252.MirrorCS", {"start": v(-125.09, 60.39) * mm, "end": v(-127.43, 58.25) * mm, "construction": true});
            skLineSegment(sketch, "E253", {"start": v(-129.03, 62.26) * mm, "end": v(-128.93, 62.35) * mm});
            skLineSegment(sketch, "E254.MirrorCS", {"start": v(-97.88, 72.4) * mm, "end": v(-98, 72.42) * mm});
            skLineSegment(sketch, "E255.MirrorCS", {"start": v(-99.11, 71.7) * mm, "end": v(-99.86, 69.18) * mm});
            skArc(sketch, "E256.MirrorCS", {"start": v(-97, 71.43) * mm, "mid": v(-97.26, 72.08) * mm, "end": v(-97.88, 72.4) * mm});
            skLineSegment(sketch, "E257.MirrorCS", {"start": v(-97, 71.43) * mm, "end": v(-96.9, 68.8) * mm});
            skArc(sketch, "E258.MirrorCS", {"start": v(-97.48, 68.28) * mm, "mid": v(-97.07, 68.4) * mm, "end": v(-96.9, 68.8) * mm});
            skLineSegment(sketch, "E259.MirrorCS", {"start": v(-100.03, 68.6) * mm, "end": v(-96.89, 68.2) * mm, "construction": true});
            skArc(sketch, "E260.MirrorCS", {"start": v(-99.86, 69.18) * mm, "mid": v(-99.8, 68.76) * mm, "end": v(-99.44, 68.53) * mm});
            skArc(sketch, "E261.MirrorCS", {"start": v(-98, 72.42) * mm, "mid": v(-98.7, 72.27) * mm, "end": v(-99.11, 71.7) * mm});
            skArc(sketch, "E262.MirrorCS", {"start": v(-91.16, 71.2) * mm, "mid": v(-91.87, 71.16) * mm, "end": v(-92.38, 70.68) * mm});
            skArc(sketch, "E263.MirrorCS", {"start": v(-90.34, 70.04) * mm, "mid": v(-90.49, 70.73) * mm, "end": v(-91.04, 71.16) * mm});
            skLineSegment(sketch, "E264.MirrorCS", {"start": v(-90.34, 70.04) * mm, "end": v(-90.7, 67.44) * mm});
            skLineSegment(sketch, "E265.MirrorCS", {"start": v(-92.38, 70.68) * mm, "end": v(-93.55, 68.32) * mm});
            skArc(sketch, "E266.MirrorCS", {"start": v(-93.55, 68.32) * mm, "mid": v(-93.57, 67.9) * mm, "end": v(-93.25, 67.61) * mm});
            skArc(sketch, "E267.MirrorCS", {"start": v(-91.36, 67.02) * mm, "mid": v(-90.94, 67.08) * mm, "end": v(-90.7, 67.44) * mm});
            skLineSegment(sketch, "E268.MirrorCS", {"start": v(-93.82, 67.79) * mm, "end": v(-90.8, 66.84) * mm, "construction": true});
            skLineSegment(sketch, "E269.MirrorCS", {"start": v(-91.04, 71.16) * mm, "end": v(-91.16, 71.2) * mm});
            skArc(sketch, "E270.MirrorCS", {"start": v(-85.58, 69.13) * mm, "mid": v(-86.28, 69.16) * mm, "end": v(-86.83, 68.72) * mm});
            skArc(sketch, "E271.MirrorCS", {"start": v(-84.86, 67.91) * mm, "mid": v(-84.94, 68.6) * mm, "end": v(-85.46, 69.08) * mm});
            skLineSegment(sketch, "E272.MirrorCS", {"start": v(-84.86, 67.91) * mm, "end": v(-85.45, 65.35) * mm});
            skLineSegment(sketch, "E273.MirrorCS", {"start": v(-86.83, 68.72) * mm, "end": v(-88.2, 66.48) * mm});
            skArc(sketch, "E274.MirrorCS", {"start": v(-88.2, 66.48) * mm, "mid": v(-88.26, 66.05) * mm, "end": v(-87.97, 65.74) * mm});
            skArc(sketch, "E275.MirrorCS", {"start": v(-86.14, 65) * mm, "mid": v(-85.71, 65) * mm, "end": v(-85.45, 65.35) * mm});
            skLineSegment(sketch, "E276.MirrorCS", {"start": v(-88.52, 65.97) * mm, "end": v(-85.59, 64.76) * mm, "construction": true});
            skLineSegment(sketch, "E277.MirrorCS", {"start": v(-85.46, 69.08) * mm, "end": v(-85.58, 69.13) * mm});
            skLineSegment(sketch, "E278.MirrorCS", {"start": v(-81.43, 66.13) * mm, "end": v(-83.18, 64.16) * mm});
            skArc(sketch, "E279.MirrorCS", {"start": v(-80.13, 66.31) * mm, "mid": v(-80.81, 66.46) * mm, "end": v(-81.43, 66.13) * mm});
            skArc(sketch, "E280.MirrorCS", {"start": v(-79.63, 64.99) * mm, "mid": v(-79.6, 65.69) * mm, "end": v(-80.02, 66.24) * mm});
            skLineSegment(sketch, "E281.MirrorCS", {"start": v(-79.63, 64.99) * mm, "end": v(-80.66, 62.56) * mm});
            skArc(sketch, "E282.MirrorCS", {"start": v(-81.4, 62.33) * mm, "mid": v(-80.98, 62.28) * mm, "end": v(-80.66, 62.56) * mm});
            skArc(sketch, "E283.MirrorCS", {"start": v(-83.18, 64.16) * mm, "mid": v(-83.3, 63.75) * mm, "end": v(-83.07, 63.39) * mm});
            skLineSegment(sketch, "E284.MirrorCS", {"start": v(-83.57, 63.7) * mm, "end": v(-80.9, 62.01) * mm, "construction": true});
            skLineSegment(sketch, "E285.MirrorCS", {"start": v(-80.02, 66.24) * mm, "end": v(-80.13, 66.31) * mm});
            skLineSegment(sketch, "E286.MirrorCS", {"start": v(-76.1, 62.4) * mm, "end": v(-78.16, 60.76) * mm});
            skArc(sketch, "E287.MirrorCS", {"start": v(-74.78, 62.35) * mm, "mid": v(-75.43, 62.61) * mm, "end": v(-76.1, 62.4) * mm});
            skArc(sketch, "E288.MirrorCS", {"start": v(-74.52, 60.96) * mm, "mid": v(-74.36, 61.64) * mm, "end": v(-74.69, 62.26) * mm});
            skLineSegment(sketch, "E289.MirrorCS", {"start": v(-74.52, 60.96) * mm, "end": v(-75.95, 58.75) * mm});
            skLineSegment(sketch, "E290.MirrorCS", {"start": v(-74.69, 62.26) * mm, "end": v(-74.78, 62.35) * mm});
            skArc(sketch, "E291.MirrorCS", {"start": v(-78.16, 60.76) * mm, "mid": v(-78.35, 60.38) * mm, "end": v(-78.18, 59.98) * mm});
            skLineSegment(sketch, "E292.MirrorCS", {"start": v(-78.63, 60.39) * mm, "end": v(-76.28, 58.25) * mm, "construction": true});
            skArc(sketch, "E293.MirrorCS", {"start": v(-76.72, 58.65) * mm, "mid": v(-76.32, 58.52) * mm, "end": v(-75.95, 58.75) * mm});
            skLineSegment(sketch, "E294.MirrorCS", {"start": v(-71.63, 58.1) * mm, "end": v(-73.95, 56.85) * mm});
            skArc(sketch, "E295.MirrorCS", {"start": v(-70.34, 57.83) * mm, "mid": v(-70.94, 58.2) * mm, "end": v(-71.63, 58.1) * mm});
            skArc(sketch, "E296.MirrorCS", {"start": v(-70.33, 56.42) * mm, "mid": v(-70.05, 57.06) * mm, "end": v(-70.27, 57.73) * mm});
            skLineSegment(sketch, "E297.MirrorCS", {"start": v(-70.33, 56.42) * mm, "end": v(-72.12, 54.5) * mm});
            skArc(sketch, "E298.MirrorCS", {"start": v(-73.95, 56.85) * mm, "mid": v(-74.2, 56.5) * mm, "end": v(-74.1, 56.1) * mm});
            skLineSegment(sketch, "E299.MirrorCS", {"start": v(-74.47, 56.57) * mm, "end": v(-72.53, 54.06) * mm, "construction": true});
            skArc(sketch, "E300.MirrorCS", {"start": v(-72.9, 54.53) * mm, "mid": v(-72.52, 54.33) * mm, "end": v(-72.12, 54.5) * mm});
            skLineSegment(sketch, "E301.MirrorCS", {"start": v(-70.27, 57.73) * mm, "end": v(-70.34, 57.83) * mm});
            skLineSegment(sketch, "E302.MirrorCS", {"start": v(-68.17, 53.22) * mm, "end": v(-70.59, 52.17) * mm});
            skArc(sketch, "E303.MirrorCS", {"start": v(-66.91, 52.83) * mm, "mid": v(-67.47, 53.26) * mm, "end": v(-68.17, 53.22) * mm});
            skArc(sketch, "E304.MirrorCS", {"start": v(-67.02, 51.42) * mm, "mid": v(-66.69, 52.04) * mm, "end": v(-66.84, 52.73) * mm});
            skLineSegment(sketch, "E305.MirrorCS", {"start": v(-67.02, 51.42) * mm, "end": v(-68.98, 49.66) * mm});
            skArc(sketch, "E306.MirrorCS", {"start": v(-69.75, 49.77) * mm, "mid": v(-69.38, 49.54) * mm, "end": v(-68.98, 49.66) * mm});
            skLineSegment(sketch, "E307.MirrorCS", {"start": v(-71.13, 51.93) * mm, "end": v(-69.42, 49.26) * mm, "construction": true});
            skArc(sketch, "E308.MirrorCS", {"start": v(-70.59, 52.17) * mm, "mid": v(-70.87, 51.85) * mm, "end": v(-70.81, 51.43) * mm});
            skLineSegment(sketch, "E309.MirrorCS", {"start": v(-66.84, 52.73) * mm, "end": v(-66.91, 52.83) * mm});
            skLineSegment(sketch, "E310.MirrorCS", {"start": v(-65.26, 47.99) * mm, "end": v(-67.82, 47.37) * mm});
            skArc(sketch, "E311.MirrorCS", {"start": v(-64.09, 47.39) * mm, "mid": v(-64.57, 47.9) * mm, "end": v(-65.26, 47.99) * mm});
            skArc(sketch, "E312.MirrorCS", {"start": v(-64.44, 46.02) * mm, "mid": v(-64, 46.57) * mm, "end": v(-64.04, 47.27) * mm});
            skLineSegment(sketch, "E313.MirrorCS", {"start": v(-64.44, 46.02) * mm, "end": v(-66.67, 44.63) * mm});
            skArc(sketch, "E314.MirrorCS", {"start": v(-67.82, 47.37) * mm, "mid": v(-68.16, 47.1) * mm, "end": v(-68.17, 46.68) * mm});
            skLineSegment(sketch, "E315.MirrorCS", {"start": v(-68.4, 47.23) * mm, "end": v(-67.18, 44.3) * mm, "construction": true});
            skArc(sketch, "E316.MirrorCS", {"start": v(-67.41, 44.86) * mm, "mid": v(-67.1, 44.57) * mm, "end": v(-66.67, 44.63) * mm});
            skLineSegment(sketch, "E317.MirrorCS", {"start": v(-64.04, 47.27) * mm, "end": v(-64.09, 47.39) * mm});
            skLineSegment(sketch, "E318.MirrorCS", {"start": v(-63.17, 42.4) * mm, "end": v(-65.8, 42.24) * mm});
            skArc(sketch, "E319.MirrorCS", {"start": v(-62.12, 41.6) * mm, "mid": v(-62.5, 42.2) * mm, "end": v(-63.17, 42.4) * mm});
            skLineSegment(sketch, "E320.MirrorCS", {"start": v(-62.1, 41.48) * mm, "end": v(-62.12, 41.6) * mm});
            skArc(sketch, "E321.MirrorCS", {"start": v(-62.7, 40.32) * mm, "mid": v(-62.18, 40.79) * mm, "end": v(-62.1, 41.48) * mm});
            skLineSegment(sketch, "E322.MirrorCS", {"start": v(-62.7, 40.32) * mm, "end": v(-65.14, 39.33) * mm});
            skArc(sketch, "E323.MirrorCS", {"start": v(-65.83, 39.7) * mm, "mid": v(-65.57, 39.36) * mm, "end": v(-65.14, 39.33) * mm});
            skLineSegment(sketch, "E324.MirrorCS", {"start": v(-66.4, 42.2) * mm, "end": v(-65.7, 39.11) * mm, "construction": true});
            skArc(sketch, "E325.MirrorCS", {"start": v(-65.8, 42.24) * mm, "mid": v(-66.18, 42.04) * mm, "end": v(-66.27, 41.62) * mm});
            skLineSegment(sketch, "E326.MirrorCS", {"start": v(-61.85, 34.3) * mm, "end": v(-64.4, 33.64) * mm});
            skArc(sketch, "E327.MirrorCS", {"start": v(-61.85, 34.3) * mm, "mid": v(-61.28, 34.7) * mm, "end": v(-61.1, 35.38) * mm});
            skLineSegment(sketch, "E328.MirrorCS", {"start": v(-61.1, 35.38) * mm, "end": v(-61.11, 35.5) * mm});
            skArc(sketch, "E329.MirrorCS", {"start": v(-61.11, 35.5) * mm, "mid": v(-61.41, 36.14) * mm, "end": v(-62.05, 36.43) * mm});
            skLineSegment(sketch, "E330.MirrorCS", {"start": v(-62.05, 36.43) * mm, "end": v(-64.68, 36.6) * mm});
            skArc(sketch, "E331.MirrorCS", {"start": v(-64.68, 36.6) * mm, "mid": v(-65.08, 36.45) * mm, "end": v(-65.22, 36.05) * mm});
            skLineSegment(sketch, "E332.MirrorCS", {"start": v(-65.28, 36.64) * mm, "end": v(-64.98, 33.49) * mm, "construction": true});
            skArc(sketch, "E333.MirrorCS", {"start": v(-65.04, 34.08) * mm, "mid": v(-64.82, 33.71) * mm, "end": v(-64.4, 33.64) * mm});
            skLineSegment(sketch, "E334.MirrorCS", {"start": v(-141.66, 26.8) * mm, "end": v(-139.03, 26.63) * mm});
            skArc(sketch, "E335.MirrorCS", {"start": v(-142.6, 27.73) * mm, "mid": v(-142.3, 27.1) * mm, "end": v(-141.66, 26.8) * mm});
            skLineSegment(sketch, "E336.MirrorCS", {"start": v(-142.61, 27.85) * mm, "end": v(-142.6, 27.73) * mm});
            skArc(sketch, "E337.MirrorCS", {"start": v(-141.86, 28.93) * mm, "mid": v(-142.43, 28.53) * mm, "end": v(-142.61, 27.85) * mm});
            skLineSegment(sketch, "E338.MirrorCS", {"start": v(-141.86, 28.93) * mm, "end": v(-139.31, 29.6) * mm});
            skArc(sketch, "E339.MirrorCS", {"start": v(-138.68, 29.15) * mm, "mid": v(-138.9, 29.52) * mm, "end": v(-139.31, 29.6) * mm});
            skLineSegment(sketch, "E340.MirrorCS", {"start": v(-138.43, 26.6) * mm, "end": v(-138.73, 29.75) * mm, "construction": true});
            skArc(sketch, "E341.MirrorCS", {"start": v(-139.03, 26.63) * mm, "mid": v(-138.63, 26.78) * mm, "end": v(-138.5, 27.19) * mm});
            skLineSegment(sketch, "E342.MirrorCS", {"start": v(-140.54, 20.84) * mm, "end": v(-137.91, 21) * mm});
            skArc(sketch, "E343.MirrorCS", {"start": v(-141.6, 21.63) * mm, "mid": v(-141.21, 21.04) * mm, "end": v(-140.54, 20.84) * mm});
            skArc(sketch, "E344.MirrorCS", {"start": v(-141, 22.92) * mm, "mid": v(-141.53, 22.45) * mm, "end": v(-141.62, 21.75) * mm});
            skLineSegment(sketch, "E345.MirrorCS", {"start": v(-141, 22.92) * mm, "end": v(-138.57, 23.9) * mm});
            skArc(sketch, "E346.MirrorCS", {"start": v(-137.88, 23.54) * mm, "mid": v(-138.14, 23.88) * mm, "end": v(-138.57, 23.9) * mm});
            skLineSegment(sketch, "E347.MirrorCS", {"start": v(-137.32, 21.03) * mm, "end": v(-138.01, 24.12) * mm, "construction": true});
            skArc(sketch, "E348.MirrorCS", {"start": v(-137.91, 21) * mm, "mid": v(-137.54, 21.2) * mm, "end": v(-137.45, 21.61) * mm});
            skLineSegment(sketch, "E349.MirrorCS", {"start": v(-141.62, 21.75) * mm, "end": v(-141.6, 21.63) * mm});
            skArc(sketch, "E350.MirrorCS", {"start": v(-136.3, 18.37) * mm, "mid": v(-136.61, 18.66) * mm, "end": v(-137.04, 18.6) * mm});
            skLineSegment(sketch, "E351.MirrorCS", {"start": v(-139.27, 17.22) * mm, "end": v(-137.04, 18.6) * mm});
            skArc(sketch, "E352.MirrorCS", {"start": v(-135.89, 15.86) * mm, "mid": v(-135.55, 16.12) * mm, "end": v(-135.54, 16.55) * mm});
            skLineSegment(sketch, "E353.MirrorCS", {"start": v(-138.45, 15.25) * mm, "end": v(-135.89, 15.86) * mm});
            skArc(sketch, "E354.MirrorCS", {"start": v(-139.62, 15.84) * mm, "mid": v(-139.15, 15.33) * mm, "end": v(-138.45, 15.25) * mm});
            skArc(sketch, "E355.MirrorCS", {"start": v(-139.27, 17.22) * mm, "mid": v(-139.7, 16.66) * mm, "end": v(-139.67, 15.96) * mm});
            skLineSegment(sketch, "E356.MirrorCS", {"start": v(-139.67, 15.96) * mm, "end": v(-139.62, 15.84) * mm});
            skLineSegment(sketch, "E357.MirrorCS", {"start": v(-135.3, 16) * mm, "end": v(-136.53, 18.93) * mm, "construction": true});
            skLineSegment(sketch, "E358.MirrorCS", {"start": v(-132.58, 11.3) * mm, "end": v(-134.3, 13.97) * mm, "construction": true});
            skArc(sketch, "E359.MirrorCS", {"start": v(-133.13, 11.06) * mm, "mid": v(-132.84, 11.38) * mm, "end": v(-132.9, 11.8) * mm});
            skLineSegment(sketch, "E360.MirrorCS", {"start": v(-135.54, 10.02) * mm, "end": v(-133.13, 11.06) * mm});
            skArc(sketch, "E361.MirrorCS", {"start": v(-136.8, 10.4) * mm, "mid": v(-136.24, 9.98) * mm, "end": v(-135.54, 10.02) * mm});
            skArc(sketch, "E362.MirrorCS", {"start": v(-136.7, 11.81) * mm, "mid": v(-137.02, 11.2) * mm, "end": v(-136.87, 10.5) * mm});
            skLineSegment(sketch, "E363.MirrorCS", {"start": v(-136.87, 10.5) * mm, "end": v(-136.8, 10.4) * mm});
            skLineSegment(sketch, "E364.MirrorCS", {"start": v(-136.7, 11.81) * mm, "end": v(-134.74, 13.57) * mm});
            skArc(sketch, "E365.MirrorCS", {"start": v(-133.97, 13.47) * mm, "mid": v(-134.33, 13.7) * mm, "end": v(-134.74, 13.57) * mm});
            skLineSegment(sketch, "E366.MirrorCS", {"start": v(-132.08, 5.13) * mm, "end": v(-129.77, 6.38) * mm});
            skArc(sketch, "E367.MirrorCS", {"start": v(-133.37, 5.4) * mm, "mid": v(-132.78, 5.03) * mm, "end": v(-132.08, 5.13) * mm});
            skArc(sketch, "E368.MirrorCS", {"start": v(-133.39, 6.82) * mm, "mid": v(-133.66, 6.17) * mm, "end": v(-133.45, 5.5) * mm});
            skLineSegment(sketch, "E369.MirrorCS", {"start": v(-133.39, 6.82) * mm, "end": v(-131.59, 8.74) * mm});
            skLineSegment(sketch, "E370.MirrorCS", {"start": v(-133.45, 5.5) * mm, "end": v(-133.37, 5.4) * mm});
            skArc(sketch, "E371.MirrorCS", {"start": v(-129.77, 6.38) * mm, "mid": v(-129.51, 6.72) * mm, "end": v(-129.6, 7.14) * mm});
            skLineSegment(sketch, "E372.MirrorCS", {"start": v(-129.24, 6.67) * mm, "end": v(-131.18, 9.18) * mm, "construction": true});
            skArc(sketch, "E373.MirrorCS", {"start": v(-130.81, 8.7) * mm, "mid": v(-131.2, 8.9) * mm, "end": v(-131.59, 8.74) * mm});
            skArc(sketch, "E374.MirrorCS", {"start": v(-126.99, 4.58) * mm, "mid": v(-127.4, 4.7) * mm, "end": v(-127.76, 4.48) * mm});
            skLineSegment(sketch, "E375.MirrorCS", {"start": v(-125.09, 2.85) * mm, "end": v(-127.43, 4.98) * mm, "construction": true});
            skArc(sketch, "E376.MirrorCS", {"start": v(-125.55, 2.48) * mm, "mid": v(-125.36, 2.86) * mm, "end": v(-125.53, 3.25) * mm});
            skLineSegment(sketch, "E377.MirrorCS", {"start": v(-127.62, 0.84) * mm, "end": v(-125.55, 2.48) * mm});
            skLineSegment(sketch, "E378.MirrorCS", {"start": v(-129.2, 2.28) * mm, "end": v(-127.76, 4.48) * mm});
            skArc(sketch, "E379.MirrorCS", {"start": v(-129.2, 2.28) * mm, "mid": v(-129.35, 1.6) * mm, "end": v(-129.03, 0.97) * mm});
            skArc(sketch, "E380.MirrorCS", {"start": v(-128.93, 0.88) * mm, "mid": v(-128.28, 0.62) * mm, "end": v(-127.62, 0.84) * mm});
            skLineSegment(sketch, "E381.MirrorCS", {"start": v(-129.03, 0.97) * mm, "end": v(-128.93, 0.88) * mm});
            skArc(sketch, "E382.MirrorCS", {"start": v(-122.31, 0.9) * mm, "mid": v(-122.74, 0.96) * mm, "end": v(-123.05, 0.67) * mm});
            skLineSegment(sketch, "E383.MirrorCS", {"start": v(-124.08, -1.75) * mm, "end": v(-123.05, 0.67) * mm});
            skLineSegment(sketch, "E384.MirrorCS", {"start": v(-122.28, -2.9) * mm, "end": v(-120.54, -0.92) * mm});
            skArc(sketch, "E385.MirrorCS", {"start": v(-120.54, -0.92) * mm, "mid": v(-120.41, -0.51) * mm, "end": v(-120.64, -0.16) * mm});
            skLineSegment(sketch, "E386.MirrorCS", {"start": v(-120.14, -0.48) * mm, "end": v(-122.82, 1.22) * mm, "construction": true});
            skArc(sketch, "E387.MirrorCS", {"start": v(-123.59, -3.08) * mm, "mid": v(-122.9, -3.23) * mm, "end": v(-122.28, -2.9) * mm});
            skLineSegment(sketch, "E388.MirrorCS", {"start": v(-123.7, -3.01) * mm, "end": v(-123.59, -3.08) * mm});
            skArc(sketch, "E389.MirrorCS", {"start": v(-124.08, -1.75) * mm, "mid": v(-124.12, -2.45) * mm, "end": v(-123.7, -3.01) * mm});
            skLineSegment(sketch, "E390.MirrorCS", {"start": v(-115.2, -2.73) * mm, "end": v(-118.13, -1.53) * mm, "construction": true});
            skArc(sketch, "E391.MirrorCS", {"start": v(-117.57, -1.76) * mm, "mid": v(-118, -1.78) * mm, "end": v(-118.26, -2.11) * mm});
            skLineSegment(sketch, "E392.MirrorCS", {"start": v(-118.86, -4.68) * mm, "end": v(-118.26, -2.11) * mm});
            skLineSegment(sketch, "E393.MirrorCS", {"start": v(-116.88, -5.49) * mm, "end": v(-115.5, -3.24) * mm});
            skArc(sketch, "E394.MirrorCS", {"start": v(-115.5, -3.24) * mm, "mid": v(-115.45, -2.82) * mm, "end": v(-115.74, -2.5) * mm});
            skArc(sketch, "E395.MirrorCS", {"start": v(-118.13, -5.9) * mm, "mid": v(-117.43, -5.92) * mm, "end": v(-116.88, -5.49) * mm});
            skLineSegment(sketch, "E396.MirrorCS", {"start": v(-118.25, -5.85) * mm, "end": v(-118.13, -5.9) * mm});
            skArc(sketch, "E397.MirrorCS", {"start": v(-118.86, -4.68) * mm, "mid": v(-118.77, -5.37) * mm, "end": v(-118.25, -5.85) * mm});
            skArc(sketch, "E398.MirrorCS", {"start": v(-112.35, -3.79) * mm, "mid": v(-112.77, -3.84) * mm, "end": v(-113, -4.2) * mm});
            skLineSegment(sketch, "E399.MirrorCS", {"start": v(-113.37, -6.81) * mm, "end": v(-113, -4.2) * mm});
            skLineSegment(sketch, "E400.MirrorCS", {"start": v(-109.9, -4.55) * mm, "end": v(-112.92, -3.61) * mm, "construction": true});
            skArc(sketch, "E401.MirrorCS", {"start": v(-110.16, -5.1) * mm, "mid": v(-110.15, -4.66) * mm, "end": v(-110.46, -4.38) * mm});
            skLineSegment(sketch, "E402.MirrorCS", {"start": v(-111.34, -7.45) * mm, "end": v(-110.16, -5.1) * mm});
            skArc(sketch, "E403.MirrorCS", {"start": v(-112.55, -7.96) * mm, "mid": v(-111.85, -7.93) * mm, "end": v(-111.34, -7.45) * mm});
            skLineSegment(sketch, "E404.MirrorCS", {"start": v(-112.67, -7.92) * mm, "end": v(-112.55, -7.96) * mm});
            skArc(sketch, "E405.MirrorCS", {"start": v(-113.37, -6.81) * mm, "mid": v(-113.22, -7.5) * mm, "end": v(-112.67, -7.92) * mm});
            skArc(sketch, "E406.MirrorCS", {"start": v(-106.23, -5.05) * mm, "mid": v(-106.64, -5.18) * mm, "end": v(-106.8, -5.57) * mm});
            skLineSegment(sketch, "E407.MirrorCS", {"start": v(-103.68, -5.38) * mm, "end": v(-106.82, -4.97) * mm, "construction": true});
            skArc(sketch, "E408.MirrorCS", {"start": v(-103.85, -5.95) * mm, "mid": v(-103.91, -5.53) * mm, "end": v(-104.27, -5.3) * mm});
            skLineSegment(sketch, "E409.MirrorCS", {"start": v(-104.6, -8.47) * mm, "end": v(-103.85, -5.95) * mm});
            skArc(sketch, "E410.MirrorCS", {"start": v(-105.7, -9.2) * mm, "mid": v(-105.02, -9.03) * mm, "end": v(-104.6, -8.47) * mm});
            skArc(sketch, "E411.MirrorCS", {"start": v(-106.72, -8.2) * mm, "mid": v(-106.45, -8.85) * mm, "end": v(-105.83, -9.17) * mm});
            skLineSegment(sketch, "E412.MirrorCS", {"start": v(-105.83, -9.17) * mm, "end": v(-105.7, -9.2) * mm});
            skArc(sketch, "E413.MirrorCS", {"start": v(-100.48, -5.92) * mm, "mid": v(-100.39, -5.5) * mm, "end": v(-100, -5.31) * mm});
            skLineSegment(sketch, "E414.MirrorCS", {"start": v(-99.96, -8.5) * mm, "end": v(-100.48, -5.92) * mm});
            skLineSegment(sketch, "E415.MirrorCS", {"start": v(-100.6, -5.33) * mm, "end": v(-97.43, -5.2) * mm, "construction": true});
            skArc(sketch, "E416.MirrorCS", {"start": v(-98.03, -5.23) * mm, "mid": v(-97.64, -5.4) * mm, "end": v(-97.5, -5.8) * mm});
            skLineSegment(sketch, "E417.MirrorCS", {"start": v(-97.83, -8.41) * mm, "end": v(-97.5, -5.8) * mm});
            skArc(sketch, "E418.MirrorCS", {"start": v(-97.83, -8.41) * mm, "mid": v(-98.14, -9.04) * mm, "end": v(-98.8, -9.3) * mm});
            skArc(sketch, "E419.MirrorCS", {"start": v(-98.92, -9.31) * mm, "mid": v(-99.59, -9.1) * mm, "end": v(-99.96, -8.5) * mm});
            skLineSegment(sketch, "E420.MirrorCS", {"start": v(-98.8, -9.3) * mm, "end": v(-98.92, -9.31) * mm});
            skArc(sketch, "E421.MirrorCS", {"start": v(-94.3, -5.15) * mm, "mid": v(-94.28, -4.72) * mm, "end": v(-93.94, -4.46) * mm});
            skLineSegment(sketch, "E422.MirrorCS", {"start": v(-93.34, -7.6) * mm, "end": v(-94.3, -5.15) * mm});
            skLineSegment(sketch, "E423.MirrorCS", {"start": v(-94.53, -4.6) * mm, "end": v(-91.43, -3.92) * mm, "construction": true});
            skArc(sketch, "E424.MirrorCS", {"start": v(-92.02, -4.04) * mm, "mid": v(-91.6, -4.14) * mm, "end": v(-91.4, -4.51) * mm});
            skLineSegment(sketch, "E425.MirrorCS", {"start": v(-91.26, -7.14) * mm, "end": v(-91.4, -4.51) * mm});
            skArc(sketch, "E426.MirrorCS", {"start": v(-92.18, -8.22) * mm, "mid": v(-92.87, -8.12) * mm, "end": v(-93.34, -7.6) * mm});
            skLineSegment(sketch, "E427.MirrorCS", {"start": v(-92.06, -8.19) * mm, "end": v(-92.18, -8.22) * mm});
            skArc(sketch, "E428.MirrorCS", {"start": v(-91.26, -7.14) * mm, "mid": v(-91.46, -7.81) * mm, "end": v(-92.06, -8.19) * mm});
            skLineSegment(sketch, "E429.MirrorCS", {"start": v(-86.83, -5.49) * mm, "end": v(-88.2, -3.24) * mm});
            skLineSegment(sketch, "E430.MirrorCS", {"start": v(-88.52, -2.73) * mm, "end": v(-85.59, -1.53) * mm, "construction": true});
            skArc(sketch, "E431.MirrorCS", {"start": v(-86.14, -1.76) * mm, "mid": v(-85.71, -1.78) * mm, "end": v(-85.45, -2.11) * mm});
            skLineSegment(sketch, "E432.MirrorCS", {"start": v(-84.86, -4.68) * mm, "end": v(-85.45, -2.11) * mm});
            skArc(sketch, "E433.MirrorCS", {"start": v(-84.86, -4.68) * mm, "mid": v(-84.94, -5.37) * mm, "end": v(-85.46, -5.85) * mm});
            skArc(sketch, "E434.MirrorCS", {"start": v(-85.58, -5.9) * mm, "mid": v(-86.28, -5.92) * mm, "end": v(-86.83, -5.49) * mm});
            skLineSegment(sketch, "E435.MirrorCS", {"start": v(-85.46, -5.85) * mm, "end": v(-85.58, -5.9) * mm});
            skLineSegment(sketch, "E436.MirrorCS", {"start": v(-81.05, -2.54) * mm, "end": v(-82.8, -0.57) * mm});
            skArc(sketch, "E437.MirrorCS", {"start": v(-79.75, -2.72) * mm, "mid": v(-80.43, -2.87) * mm, "end": v(-81.05, -2.54) * mm});
            skArc(sketch, "E438.MirrorCS", {"start": v(-79.25, -1.4) * mm, "mid": v(-79.21, -2.1) * mm, "end": v(-79.64, -2.65) * mm});
            skLineSegment(sketch, "E439.MirrorCS", {"start": v(-79.25, -1.4) * mm, "end": v(-80.28, 1.02) * mm});
            skArc(sketch, "E440.MirrorCS", {"start": v(-81.02, 1.26) * mm, "mid": v(-80.6, 1.31) * mm, "end": v(-80.28, 1.02) * mm});
            skLineSegment(sketch, "E441.MirrorCS", {"start": v(-83.2, -0.12) * mm, "end": v(-80.51, 1.58) * mm, "construction": true});
            skArc(sketch, "E442.MirrorCS", {"start": v(-82.8, -0.57) * mm, "mid": v(-82.92, -0.16) * mm, "end": v(-82.69, 0.2) * mm});
            skLineSegment(sketch, "E443.MirrorCS", {"start": v(-79.64, -2.65) * mm, "end": v(-79.75, -2.72) * mm});
            skArc(sketch, "E444.MirrorCS", {"start": v(-74.78, 0.88) * mm, "mid": v(-75.43, 0.62) * mm, "end": v(-76.1, 0.84) * mm});
            skArc(sketch, "E445.MirrorCS", {"start": v(-74.52, 2.28) * mm, "mid": v(-74.36, 1.6) * mm, "end": v(-74.69, 0.97) * mm});
            skLineSegment(sketch, "E446.MirrorCS", {"start": v(-76.1, 0.84) * mm, "end": v(-78.16, 2.48) * mm});
            skLineSegment(sketch, "E447.MirrorCS", {"start": v(-74.52, 2.28) * mm, "end": v(-75.95, 4.48) * mm});
            skArc(sketch, "E448.MirrorCS", {"start": v(-78.16, 2.48) * mm, "mid": v(-78.35, 2.86) * mm, "end": v(-78.18, 3.25) * mm});
            skLineSegment(sketch, "E449.MirrorCS", {"start": v(-78.63, 2.85) * mm, "end": v(-76.28, 4.98) * mm, "construction": true});
            skArc(sketch, "E450.MirrorCS", {"start": v(-76.72, 4.58) * mm, "mid": v(-76.32, 4.7) * mm, "end": v(-75.95, 4.48) * mm});
            skArc(sketch, "E451.MirrorCS", {"start": v(-70.34, 5.4) * mm, "mid": v(-70.94, 5.03) * mm, "end": v(-71.63, 5.13) * mm});
            skArc(sketch, "E452.MirrorCS", {"start": v(-70.33, 6.82) * mm, "mid": v(-70.05, 6.17) * mm, "end": v(-70.27, 5.5) * mm});
            skLineSegment(sketch, "E453.MirrorCS", {"start": v(-70.27, 5.5) * mm, "end": v(-70.34, 5.4) * mm});
            skLineSegment(sketch, "E454.MirrorCS", {"start": v(-71.63, 5.13) * mm, "end": v(-73.95, 6.38) * mm});
            skLineSegment(sketch, "E455.MirrorCS", {"start": v(-70.33, 6.82) * mm, "end": v(-72.12, 8.74) * mm});
            skArc(sketch, "E456.MirrorCS", {"start": v(-73.95, 6.38) * mm, "mid": v(-74.2, 6.72) * mm, "end": v(-74.1, 7.14) * mm});
            skLineSegment(sketch, "E457.MirrorCS", {"start": v(-74.47, 6.67) * mm, "end": v(-72.53, 9.18) * mm, "construction": true});
            skArc(sketch, "E458.MirrorCS", {"start": v(-72.9, 8.7) * mm, "mid": v(-72.52, 8.9) * mm, "end": v(-72.12, 8.74) * mm});
            skLineSegment(sketch, "E459.MirrorCS", {"start": v(-68.17, 10.02) * mm, "end": v(-70.59, 11.06) * mm});
            skArc(sketch, "E460.MirrorCS", {"start": v(-66.91, 10.4) * mm, "mid": v(-67.47, 9.98) * mm, "end": v(-68.17, 10.02) * mm});
            skArc(sketch, "E461.MirrorCS", {"start": v(-67.02, 11.81) * mm, "mid": v(-66.69, 11.2) * mm, "end": v(-66.84, 10.5) * mm});
            skLineSegment(sketch, "E462.MirrorCS", {"start": v(-66.84, 10.5) * mm, "end": v(-66.91, 10.4) * mm});
            skLineSegment(sketch, "E463.MirrorCS", {"start": v(-67.02, 11.81) * mm, "end": v(-68.98, 13.57) * mm});
            skArc(sketch, "E464.MirrorCS", {"start": v(-70.59, 11.06) * mm, "mid": v(-70.87, 11.38) * mm, "end": v(-70.81, 11.8) * mm});
            skLineSegment(sketch, "E465.MirrorCS", {"start": v(-71.13, 11.3) * mm, "end": v(-69.42, 13.97) * mm, "construction": true});
            skArc(sketch, "E466.MirrorCS", {"start": v(-69.75, 13.47) * mm, "mid": v(-69.38, 13.7) * mm, "end": v(-68.98, 13.57) * mm});
            skLineSegment(sketch, "E467.MirrorCS", {"start": v(-65.18, 15.42) * mm, "end": v(-67.74, 16.03) * mm});
            skArc(sketch, "E468.MirrorCS", {"start": v(-67.74, 16.03) * mm, "mid": v(-68.07, 16.3) * mm, "end": v(-68.09, 16.72) * mm});
            skLineSegment(sketch, "E469.MirrorCS", {"start": v(-68.32, 16.17) * mm, "end": v(-67.1, 19.1) * mm, "construction": true});
            skArc(sketch, "E470.MirrorCS", {"start": v(-67.33, 18.54) * mm, "mid": v(-67.01, 18.83) * mm, "end": v(-66.59, 18.78) * mm});
            skLineSegment(sketch, "E471.MirrorCS", {"start": v(-64.35, 17.39) * mm, "end": v(-66.59, 18.78) * mm});
            skArc(sketch, "E472.MirrorCS", {"start": v(-64.35, 17.39) * mm, "mid": v(-63.92, 16.83) * mm, "end": v(-63.95, 16.13) * mm});
            skLineSegment(sketch, "E473.MirrorCS", {"start": v(-63.95, 16.13) * mm, "end": v(-64, 16.02) * mm});
            skArc(sketch, "E474.MirrorCS", {"start": v(-64, 16.02) * mm, "mid": v(-64.48, 15.5) * mm, "end": v(-65.18, 15.42) * mm});
            skLineSegment(sketch, "E475.MirrorCS", {"start": v(-63.04, 21.42) * mm, "end": v(-65.67, 21.58) * mm});
            skArc(sketch, "E476.MirrorCS", {"start": v(-61.99, 22.21) * mm, "mid": v(-62.37, 21.62) * mm, "end": v(-63.04, 21.42) * mm});
            skLineSegment(sketch, "E477.MirrorCS", {"start": v(-61.96, 22.34) * mm, "end": v(-61.99, 22.21) * mm});
            skArc(sketch, "E478.MirrorCS", {"start": v(-62.57, 23.5) * mm, "mid": v(-62.05, 23.03) * mm, "end": v(-61.96, 22.34) * mm});
            skLineSegment(sketch, "E479.MirrorCS", {"start": v(-62.57, 23.5) * mm, "end": v(-65.01, 24.48) * mm});
            skArc(sketch, "E480.MirrorCS", {"start": v(-65.7, 24.12) * mm, "mid": v(-65.44, 24.46) * mm, "end": v(-65.01, 24.48) * mm});
            skLineSegment(sketch, "E481.MirrorCS", {"start": v(-66.27, 21.61) * mm, "end": v(-65.57, 24.7) * mm, "construction": true});
            skArc(sketch, "E482.MirrorCS", {"start": v(-65.67, 21.58) * mm, "mid": v(-66.04, 21.78) * mm, "end": v(-66.13, 22.2) * mm});
            skArc(sketch, "E483.MirrorCS", {"start": v(-61.05, 28.32) * mm, "mid": v(-61.36, 27.69) * mm, "end": v(-62, 27.4) * mm});
            skLineSegment(sketch, "E484.MirrorCS", {"start": v(-62, 27.4) * mm, "end": v(-64.62, 27.23) * mm});
            skArc(sketch, "E485.MirrorCS", {"start": v(-64.62, 27.23) * mm, "mid": v(-65.02, 27.38) * mm, "end": v(-65.16, 27.78) * mm});
            skLineSegment(sketch, "E486.MirrorCS", {"start": v(-65.22, 27.19) * mm, "end": v(-64.92, 30.34) * mm, "construction": true});
            skArc(sketch, "E487.MirrorCS", {"start": v(-64.98, 29.75) * mm, "mid": v(-64.76, 30.12) * mm, "end": v(-64.34, 30.2) * mm});
            skLineSegment(sketch, "E488.MirrorCS", {"start": v(-61.8, 29.53) * mm, "end": v(-64.34, 30.2) * mm});
            skArc(sketch, "E489.MirrorCS", {"start": v(-61.8, 29.53) * mm, "mid": v(-61.22, 29.13) * mm, "end": v(-61.04, 28.45) * mm});
            skLineSegment(sketch, "E490.MirrorCS", {"start": v(-61.04, 28.45) * mm, "end": v(-61.05, 28.32) * mm});
            skLineSegment(sketch, "E491.MirrorCS", {"start": v(-106.72, -8.2) * mm, "end": v(-106.8, -5.57) * mm});
            skLineSegment(sketch, "E492.MirrorCS", {"start": v(-74.69, 0.97) * mm, "end": v(-74.78, 0.88) * mm});
            skArc(sketch, "E493.MirrorCS", {"start": v(-88.2, -3.24) * mm, "mid": v(-88.26, -2.82) * mm, "end": v(-87.97, -2.5) * mm});
            skLineSegment(sketch, "E494.0", {"start": v(-1.94, 16.87) * mm, "end": v(-1.94, 34.75) * mm, "construction": true});
            skSolve(sketch);
        }
        {
            var Q0;
            Q0=makeQuery(id+"F0.imprint","IMPRINT",FACE,{"disambiguationData":[TD([[makeQuery(id+"F0.imprint","IMPRINT",EDGE,{"derivedFrom":sQuery(id+"F0.wireOp",EDGE,"E3")}),-1.0]])]});
            var Q1;
            {var subQ1=sQuery(id+"F0.wireOp",EDGE,"E29");var subQ3=sQuery(id+"F0.wireOp",EDGE,"E1");var subQ4=makeQuery(id+"F0.imprint","INTERSECT",VERTEX,{"derivedFrom":[subQ3,subQ1]});Q1=makeQuery(id+"F0.imprint","IMPRINT",FACE,{"disambiguationData":[TD([[makeQuery(id+"F0.imprint","IMPRINT",EDGE,{"disambiguationData":[TD([[subQ4,-1.0]])],"derivedFrom":subQ3}),1.0]])]});}
            var Q2;
            Q2=makeQuery(id+"F0.imprint","IMPRINT",FACE,{"disambiguationData":[TD([[makeQuery(id+"F0.imprint","IMPRINT",EDGE,{"derivedFrom":sQuery(id+"F0.wireOp",EDGE,"E27")}),-1.0]])]});
            var Q3;
            Q3=makeQuery(id+"F0.imprint","IMPRINT",FACE,{"disambiguationData":[TD([[makeQuery(id+"F0.imprint","IMPRINT",EDGE,{"derivedFrom":sQuery(id+"F0.wireOp",EDGE,"E35")}),-1.0]])]});
            var Q4;
            Q4=makeQuery(id+"F0.imprint","IMPRINT",FACE,{"disambiguationData":[TD([[makeQuery(id+"F0.imprint","IMPRINT",EDGE,{"derivedFrom":sQuery(id+"F0.wireOp",EDGE,"E44")}),-1.0]])]});
            var Q5;
            {var subQ1=sQuery(id+"F0.wireOp",EDGE,"E28");var subQ8=sQuery(id+"F0.wireOp",EDGE,"E1");var subQ10=makeQuery(id+"F0.imprint","INTERSECT",VERTEX,{"derivedFrom":[subQ8,subQ1]});Q5=makeQuery(id+"F0.imprint","IMPRINT",FACE,{"disambiguationData":[TD([[makeQuery(id+"F0.imprint","IMPRINT",EDGE,{"disambiguationData":[TD([[subQ10,-1.0]])],"derivedFrom":subQ8}),1.0]])]});}
            var Q6;
            {var subQ1=sQuery(id+"F0.wireOp",EDGE,"E37");var subQ3=sQuery(id+"F0.wireOp",EDGE,"E1");var subQ4=makeQuery(id+"F0.imprint","INTERSECT",VERTEX,{"derivedFrom":[subQ3,subQ1]});Q6=makeQuery(id+"F0.imprint","IMPRINT",FACE,{"disambiguationData":[TD([[makeQuery(id+"F0.imprint","IMPRINT",EDGE,{"disambiguationData":[TD([[subQ4,-1.0]])],"derivedFrom":subQ3}),1.0]])]});}
            var Q7;
            {var subQ1=sQuery(id+"F0.wireOp",EDGE,"E36");var subQ8=sQuery(id+"F0.wireOp",EDGE,"E1");var subQ10=makeQuery(id+"F0.imprint","INTERSECT",VERTEX,{"derivedFrom":[subQ8,subQ1]});Q7=makeQuery(id+"F0.imprint","IMPRINT",FACE,{"disambiguationData":[TD([[makeQuery(id+"F0.imprint","IMPRINT",EDGE,{"disambiguationData":[TD([[subQ10,-1.0]])],"derivedFrom":subQ8}),1.0]])]});}
            var Q8;
            {var subQ1=sQuery(id+"F0.wireOp",EDGE,"E45");var subQ8=sQuery(id+"F0.wireOp",EDGE,"E1");var subQ10=makeQuery(id+"F0.imprint","INTERSECT",VERTEX,{"derivedFrom":[subQ8,subQ1]});Q8=makeQuery(id+"F0.imprint","IMPRINT",FACE,{"disambiguationData":[TD([[makeQuery(id+"F0.imprint","IMPRINT",EDGE,{"disambiguationData":[TD([[subQ10,-1.0]])],"derivedFrom":subQ8}),1.0]])]});}
            var Q9;
            {var subQ3=sQuery(id+"F0.wireOp",EDGE,"E1");var subQ9=sQuery(id+"F0.wireOp",EDGE,"E10");var subQ11=makeQuery(id+"F0.imprint","INTERSECT",VERTEX,{"derivedFrom":[subQ3,subQ9]});Q9=makeQuery(id+"F0.imprint","IMPRINT",FACE,{"disambiguationData":[TD([[makeQuery(id+"F0.imprint","IMPRINT",EDGE,{"disambiguationData":[TD([[subQ11,1.0]])],"derivedFrom":subQ3}),1.0]])]});}
            var Q10;
            Q10=makeQuery(id+"F0.imprint","IMPRINT",FACE,{"disambiguationData":[TD([[makeQuery(id+"F0.imprint","IMPRINT",EDGE,{"derivedFrom":sQuery(id+"F0.wireOp",EDGE,"E8")}),-1.0]])]});
            var Q11;
            Q11=makeQuery(id+"F0.imprint","IMPRINT",FACE,{"disambiguationData":[TD([[makeQuery(id+"F0.imprint","IMPRINT",EDGE,{"derivedFrom":sQuery(id+"F0.wireOp",EDGE,"E18")}),-1.0]])]});
            var Q12;
            {var subQ1=sQuery(id+"F0.wireOp",EDGE,"E19");var subQ9=sQuery(id+"F0.wireOp",EDGE,"E1");var subQ11=makeQuery(id+"F0.imprint","INTERSECT",VERTEX,{"derivedFrom":[subQ9,subQ1]});Q12=makeQuery(id+"F0.imprint","IMPRINT",FACE,{"disambiguationData":[TD([[makeQuery(id+"F0.imprint","IMPRINT",EDGE,{"disambiguationData":[TD([[subQ11,-1.0]])],"derivedFrom":subQ9}),1.0]])]});}
            var Q13;
            {var subQ5=sQuery(id+"F0.wireOp",EDGE,"E1");var subQ9=sQuery(id+"F0.wireOp",EDGE,"E46");var subQ11=makeQuery(id+"F0.imprint","INTERSECT",VERTEX,{"derivedFrom":[subQ5,subQ9]});Q13=makeQuery(id+"F0.imprint","IMPRINT",FACE,{"disambiguationData":[TD([[makeQuery(id+"F0.imprint","IMPRINT",EDGE,{"disambiguationData":[TD([[subQ11,-1.0]])],"derivedFrom":subQ5}),1.0]])]});}
            var Q14;
            {var subQ1=sQuery(id+"F0.wireOp",EDGE,"E10");var subQ3=sQuery(id+"F0.wireOp",EDGE,"E1");var subQ4=makeQuery(id+"F0.imprint","INTERSECT",VERTEX,{"derivedFrom":[subQ3,subQ1]});Q14=makeQuery(id+"F0.imprint","IMPRINT",FACE,{"disambiguationData":[TD([[makeQuery(id+"F0.imprint","IMPRINT",EDGE,{"disambiguationData":[TD([[subQ4,-1.0]])],"derivedFrom":subQ3}),1.0]])]});}
            var Q15;
            {var subQ1=sQuery(id+"F0.wireOp",EDGE,"E9");var subQ9=sQuery(id+"F0.wireOp",EDGE,"E1");var subQ11=makeQuery(id+"F0.imprint","INTERSECT",VERTEX,{"derivedFrom":[subQ9,subQ1]});Q15=makeQuery(id+"F0.imprint","IMPRINT",FACE,{"disambiguationData":[TD([[makeQuery(id+"F0.imprint","IMPRINT",EDGE,{"disambiguationData":[TD([[subQ11,1.0]])],"derivedFrom":subQ9}),1.0]])]});}
            var Q16;
            {var subQ3=sQuery(id+"F0.wireOp",EDGE,"E1");var subQ6=sQuery(id+"F0.wireOp",EDGE,"E110.MirrorCS");var subQ8=makeQuery(id+"F0.imprint","INTERSECT",VERTEX,{"derivedFrom":[subQ3,subQ6]});Q16=makeQuery(id+"F0.imprint","IMPRINT",FACE,{"disambiguationData":[TD([[makeQuery(id+"F0.imprint","IMPRINT",EDGE,{"disambiguationData":[TD([[subQ8,-1.0]])],"derivedFrom":subQ3}),1.0]])]});}
            var Q17;
            {var subQ1=sQuery(id+"F0.wireOp",EDGE,"E111.MirrorCS");Q17=makeQuery(id+"F0.imprint","IMPRINT",FACE,{"disambiguationData":[TD([[makeQuery(id+"F0.imprint","IMPRINT",EDGE,{"derivedFrom":subQ1}),-1.0]])]});}
            var Q18;
            {var subQ0=sQuery(id+"F0.wireOp",EDGE,"3ecdae54-af57-4552-93a2-1e5ff7a8caf50.MirrorCS");var subQ3=sQuery(id+"F0.wireOp",EDGE,"E1");var subQ4=makeQuery(id+"F0.imprint","INTERSECT",VERTEX,{"derivedFrom":[subQ3,subQ0]});Q18=makeQuery(id+"F0.imprint","IMPRINT",FACE,{"disambiguationData":[TD([[makeQuery(id+"F0.imprint","IMPRINT",EDGE,{"disambiguationData":[TD([[subQ4,-1.0]])],"derivedFrom":subQ3}),1.0]])]});}
            var Q19;
            {var subQ1=sQuery(id+"F0.wireOp",EDGE,"65967323-df29-41a9-93c0-9a3df9e9e95e0.MirrorCS");var subQ3=sQuery(id+"F0.wireOp",EDGE,"E1");var subQ4=makeQuery(id+"F0.imprint","INTERSECT",VERTEX,{"derivedFrom":[subQ3,subQ1]});Q19=makeQuery(id+"F0.imprint","IMPRINT",FACE,{"disambiguationData":[TD([[makeQuery(id+"F0.imprint","IMPRINT",EDGE,{"disambiguationData":[TD([[subQ4,-1.0]])],"derivedFrom":subQ3}),1.0]])]});}
            var Q20;
            {var subQ3=sQuery(id+"F0.wireOp",EDGE,"E1");var subQ9=sQuery(id+"F0.wireOp",EDGE,"65967323-df29-41a9-93c0-9a3df9e9e95e0.MirrorCS");var subQ10=makeQuery(id+"F0.imprint","INTERSECT",VERTEX,{"derivedFrom":[subQ3,subQ9]});Q20=makeQuery(id+"F0.imprint","IMPRINT",FACE,{"disambiguationData":[TD([[makeQuery(id+"F0.imprint","IMPRINT",EDGE,{"disambiguationData":[TD([[subQ10,1.0]])],"derivedFrom":subQ3}),1.0]])]});}
            var Q21;
            {var subQ1=sQuery(id+"F0.wireOp",EDGE,"E104.MirrorCS");var subQ7=sQuery(id+"F0.wireOp",EDGE,"E1");var subQ8=makeQuery(id+"F0.imprint","INTERSECT",VERTEX,{"derivedFrom":[subQ7,subQ1]});Q21=makeQuery(id+"F0.imprint","IMPRINT",FACE,{"disambiguationData":[TD([[makeQuery(id+"F0.imprint","IMPRINT",EDGE,{"disambiguationData":[TD([[subQ8,-1.0]])],"derivedFrom":subQ7}),1.0]])]});}
            var Q22;
            {var subQ1=sQuery(id+"F0.wireOp",EDGE,"E103.MirrorCS");Q22=makeQuery(id+"F0.imprint","IMPRINT",FACE,{"disambiguationData":[TD([[makeQuery(id+"F0.imprint","IMPRINT",EDGE,{"derivedFrom":subQ1}),-1.0]])]});}
            var Q23;
            {var subQ1=sQuery(id+"F0.wireOp",EDGE,"E98.MirrorCS");var subQ5=sQuery(id+"F0.wireOp",EDGE,"E1");var subQ6=makeQuery(id+"F0.imprint","INTERSECT",VERTEX,{"derivedFrom":[subQ5,subQ1]});Q23=makeQuery(id+"F0.imprint","IMPRINT",FACE,{"disambiguationData":[TD([[makeQuery(id+"F0.imprint","IMPRINT",EDGE,{"disambiguationData":[TD([[subQ6,-1.0]])],"derivedFrom":subQ5}),1.0]])]});}
            var Q24;
            {var subQ1=sQuery(id+"F0.wireOp",EDGE,"E99.MirrorCS");var subQ3=sQuery(id+"F0.wireOp",EDGE,"E1");var subQ4=makeQuery(id+"F0.imprint","INTERSECT",VERTEX,{"derivedFrom":[subQ3,subQ1]});Q24=makeQuery(id+"F0.imprint","IMPRINT",FACE,{"disambiguationData":[TD([[makeQuery(id+"F0.imprint","IMPRINT",EDGE,{"disambiguationData":[TD([[subQ4,-1.0]])],"derivedFrom":subQ3}),1.0]])]});}
            var Q25;
            {var subQ6=sQuery(id+"F0.wireOp",EDGE,"E96.MirrorCS");Q25=makeQuery(id+"F0.imprint","IMPRINT",FACE,{"disambiguationData":[TD([[makeQuery(id+"F0.imprint","IMPRINT",EDGE,{"derivedFrom":subQ6}),-1.0]])]});}
            var Q26;
            {var subQ1=sQuery(id+"F0.wireOp",EDGE,"E92.MirrorCS");var subQ9=sQuery(id+"F0.wireOp",EDGE,"E1");var subQ10=makeQuery(id+"F0.imprint","INTERSECT",VERTEX,{"derivedFrom":[subQ9,subQ1]});Q26=makeQuery(id+"F0.imprint","IMPRINT",FACE,{"disambiguationData":[TD([[makeQuery(id+"F0.imprint","IMPRINT",EDGE,{"disambiguationData":[TD([[subQ10,-1.0]])],"derivedFrom":subQ9}),1.0]])]});}
            var Q27;
            {var subQ3=sQuery(id+"F0.wireOp",EDGE,"E1");var subQ6=sQuery(id+"F0.wireOp",EDGE,"E89.MirrorCS");var subQ8=makeQuery(id+"F0.imprint","INTERSECT",VERTEX,{"derivedFrom":[subQ3,subQ6]});Q27=makeQuery(id+"F0.imprint","IMPRINT",FACE,{"disambiguationData":[TD([[makeQuery(id+"F0.imprint","IMPRINT",EDGE,{"disambiguationData":[TD([[subQ8,-1.0]])],"derivedFrom":subQ3}),1.0]])]});}
            var Q28;
            {var subQ1=sQuery(id+"F0.wireOp",EDGE,"E90.MirrorCS");Q28=makeQuery(id+"F0.imprint","IMPRINT",FACE,{"disambiguationData":[TD([[makeQuery(id+"F0.imprint","IMPRINT",EDGE,{"derivedFrom":subQ1}),-1.0]])]});}
            var Q29;
            {var subQ3=sQuery(id+"F0.wireOp",EDGE,"E1");var subQ9=sQuery(id+"F0.wireOp",EDGE,"E118.MirrorCS");var subQ10=makeQuery(id+"F0.imprint","INTERSECT",VERTEX,{"derivedFrom":[subQ3,subQ9]});Q29=makeQuery(id+"F0.imprint","IMPRINT",FACE,{"disambiguationData":[TD([[makeQuery(id+"F0.imprint","IMPRINT",EDGE,{"disambiguationData":[TD([[subQ10,-1.0]])],"derivedFrom":subQ3}),1.0]])]});}
            var Q30;
            {var subQ5=sQuery(id+"F0.wireOp",EDGE,"E122.MirrorCS");var subQ6=sQuery(id+"F0.wireOp",EDGE,"E1");var subQ7=makeQuery(id+"F0.imprint","INTERSECT",VERTEX,{"derivedFrom":[subQ6,subQ5]});Q30=makeQuery(id+"F0.imprint","IMPRINT",FACE,{"disambiguationData":[TD([[makeQuery(id+"F0.imprint","IMPRINT",EDGE,{"disambiguationData":[TD([[subQ7,-1.0]])],"derivedFrom":subQ6}),1.0]])]});}
            var Q31;
            {var subQ4=sQuery(id+"F0.wireOp",EDGE,"0ff8bcd8-736d-4c19-bfa1-dbbcef77a4710.MirrorCS");Q31=makeQuery(id+"F0.imprint","IMPRINT",FACE,{"disambiguationData":[TD([[makeQuery(id+"F0.imprint","IMPRINT",EDGE,{"derivedFrom":subQ4}),1.0]])]});}
            var Q32;
            {var subQ3=sQuery(id+"F0.wireOp",EDGE,"E1");var subQ5=sQuery(id+"F0.wireOp",EDGE,"E125.MirrorCS");var subQ6=makeQuery(id+"F0.imprint","INTERSECT",VERTEX,{"derivedFrom":[subQ3,subQ5]});Q32=makeQuery(id+"F0.imprint","IMPRINT",FACE,{"disambiguationData":[TD([[makeQuery(id+"F0.imprint","IMPRINT",EDGE,{"disambiguationData":[TD([[subQ6,-1.0]])],"derivedFrom":subQ3}),1.0]])]});}
            var Q33;
            {var subQ4=sQuery(id+"F0.wireOp",EDGE,"E123.MirrorCS");Q33=makeQuery(id+"F0.imprint","IMPRINT",FACE,{"disambiguationData":[TD([[makeQuery(id+"F0.imprint","IMPRINT",EDGE,{"derivedFrom":subQ4}),1.0]])]});}
            var Q34;
            {var subQ3=sQuery(id+"F0.wireOp",EDGE,"E1");var subQ9=sQuery(id+"F0.wireOp",EDGE,"E130.MirrorCS");var subQ10=makeQuery(id+"F0.imprint","INTERSECT",VERTEX,{"derivedFrom":[subQ3,subQ9]});Q34=makeQuery(id+"F0.imprint","IMPRINT",FACE,{"disambiguationData":[TD([[makeQuery(id+"F0.imprint","IMPRINT",EDGE,{"disambiguationData":[TD([[subQ10,-1.0]])],"derivedFrom":subQ3}),1.0]])]});}
            var Q35;
            {var subQ1=sQuery(id+"F0.wireOp",EDGE,"E133.MirrorCS");var subQ3=sQuery(id+"F0.wireOp",EDGE,"E1");var subQ4=makeQuery(id+"F0.imprint","INTERSECT",VERTEX,{"derivedFrom":[subQ3,subQ1]});Q35=makeQuery(id+"F0.imprint","IMPRINT",FACE,{"disambiguationData":[TD([[makeQuery(id+"F0.imprint","IMPRINT",EDGE,{"disambiguationData":[TD([[subQ4,-1.0]])],"derivedFrom":subQ3}),1.0]])]});}
            var Q36;
            {var subQ0=sQuery(id+"F0.wireOp",EDGE,"E131.MirrorCS");Q36=makeQuery(id+"F0.imprint","IMPRINT",FACE,{"disambiguationData":[TD([[makeQuery(id+"F0.imprint","IMPRINT",EDGE,{"derivedFrom":subQ0}),1.0]])]});}
            var Q37;
            {var subQ3=sQuery(id+"F0.wireOp",EDGE,"E1");var subQ5=sQuery(id+"F0.wireOp",EDGE,"E137.MirrorCS");var subQ6=makeQuery(id+"F0.imprint","INTERSECT",VERTEX,{"derivedFrom":[subQ3,subQ5]});Q37=makeQuery(id+"F0.imprint","IMPRINT",FACE,{"disambiguationData":[TD([[makeQuery(id+"F0.imprint","IMPRINT",EDGE,{"disambiguationData":[TD([[subQ6,-1.0]])],"derivedFrom":subQ3}),1.0]])]});}
            var Q38;
            {var subQ7=sQuery(id+"F0.wireOp",EDGE,"E1");var subQ9=sQuery(id+"F0.wireOp",EDGE,"E126.MirrorCS");var subQ10=makeQuery(id+"F0.imprint","INTERSECT",VERTEX,{"derivedFrom":[subQ7,subQ9]});Q38=makeQuery(id+"F0.imprint","IMPRINT",FACE,{"disambiguationData":[TD([[makeQuery(id+"F0.imprint","IMPRINT",EDGE,{"disambiguationData":[TD([[subQ10,-1.0]])],"derivedFrom":subQ7}),1.0]])]});}
            var Q39;
            {var subQ1=sQuery(id+"F0.wireOp",EDGE,"E140.MirrorCS");var subQ3=sQuery(id+"F0.wireOp",EDGE,"E1");var subQ4=makeQuery(id+"F0.imprint","INTERSECT",VERTEX,{"derivedFrom":[subQ3,subQ1]});Q39=makeQuery(id+"F0.imprint","IMPRINT",FACE,{"disambiguationData":[TD([[makeQuery(id+"F0.imprint","IMPRINT",EDGE,{"disambiguationData":[TD([[subQ4,-1.0]])],"derivedFrom":subQ3}),1.0]])]});}
            var Q40;
            {var subQ0=sQuery(id+"F0.wireOp",EDGE,"E138.MirrorCS");Q40=makeQuery(id+"F0.imprint","IMPRINT",FACE,{"disambiguationData":[TD([[makeQuery(id+"F0.imprint","IMPRINT",EDGE,{"derivedFrom":subQ0}),1.0]])]});}
            var Q41;
            {var subQ1=sQuery(id+"F0.wireOp",EDGE,"E146.MirrorCS");var subQ3=sQuery(id+"F0.wireOp",EDGE,"E1");var subQ4=makeQuery(id+"F0.imprint","INTERSECT",VERTEX,{"derivedFrom":[subQ3,subQ1]});Q41=makeQuery(id+"F0.imprint","IMPRINT",FACE,{"disambiguationData":[TD([[makeQuery(id+"F0.imprint","IMPRINT",EDGE,{"disambiguationData":[TD([[subQ4,-1.0]])],"derivedFrom":subQ3}),1.0]])]});}
            var Q42;
            {var subQ0=sQuery(id+"F0.wireOp",EDGE,"E144.MirrorCS");Q42=makeQuery(id+"F0.imprint","IMPRINT",FACE,{"disambiguationData":[TD([[makeQuery(id+"F0.imprint","IMPRINT",EDGE,{"derivedFrom":subQ0}),1.0]])]});}
            var Q43;
            {var subQ3=sQuery(id+"F0.wireOp",EDGE,"E1");var subQ7=sQuery(id+"F0.wireOp",EDGE,"E143.MirrorCS");var subQ8=makeQuery(id+"F0.imprint","INTERSECT",VERTEX,{"derivedFrom":[subQ3,subQ7]});Q43=makeQuery(id+"F0.imprint","IMPRINT",FACE,{"disambiguationData":[TD([[makeQuery(id+"F0.imprint","IMPRINT",EDGE,{"disambiguationData":[TD([[subQ8,-1.0]])],"derivedFrom":subQ3}),1.0]])]});}
            var Q44;
            {var subQ1=sQuery(id+"F0.wireOp",EDGE,"E82.MirrorCS");var subQ3=sQuery(id+"F0.wireOp",EDGE,"E1");var subQ4=makeQuery(id+"F0.imprint","INTERSECT",VERTEX,{"derivedFrom":[subQ3,subQ1]});Q44=makeQuery(id+"F0.imprint","IMPRINT",FACE,{"disambiguationData":[TD([[makeQuery(id+"F0.imprint","IMPRINT",EDGE,{"disambiguationData":[TD([[subQ4,-1.0]])],"derivedFrom":subQ3}),1.0]])]});}
            var Q45;
            {var subQ6=sQuery(id+"F0.wireOp",EDGE,"E83.MirrorCS");Q45=makeQuery(id+"F0.imprint","IMPRINT",FACE,{"disambiguationData":[TD([[makeQuery(id+"F0.imprint","IMPRINT",EDGE,{"derivedFrom":subQ6}),-1.0]])]});}
            var Q46;
            {var subQ1=sQuery(id+"F0.wireOp",EDGE,"E85.MirrorCS");var subQ5=sQuery(id+"F0.wireOp",EDGE,"E1");var subQ6=makeQuery(id+"F0.imprint","INTERSECT",VERTEX,{"derivedFrom":[subQ5,subQ1]});Q46=makeQuery(id+"F0.imprint","IMPRINT",FACE,{"disambiguationData":[TD([[makeQuery(id+"F0.imprint","IMPRINT",EDGE,{"disambiguationData":[TD([[subQ6,-1.0]])],"derivedFrom":subQ5}),1.0]])]});}
            var Q47;
            {var subQ1=sQuery(id+"F0.wireOp",EDGE,"E79.MirrorCS");var subQ3=sQuery(id+"F0.wireOp",EDGE,"E1");var subQ4=makeQuery(id+"F0.imprint","INTERSECT",VERTEX,{"derivedFrom":[subQ3,subQ1]});Q47=makeQuery(id+"F0.imprint","IMPRINT",FACE,{"disambiguationData":[TD([[makeQuery(id+"F0.imprint","IMPRINT",EDGE,{"disambiguationData":[TD([[subQ4,-1.0]])],"derivedFrom":subQ3}),1.0]])]});}
            var Q48;
            {var subQ1=sQuery(id+"F0.wireOp",EDGE,"E77.MirrorCS");Q48=makeQuery(id+"F0.imprint","IMPRINT",FACE,{"disambiguationData":[TD([[makeQuery(id+"F0.imprint","IMPRINT",EDGE,{"derivedFrom":subQ1}),-1.0]])]});}
            var Q49;
            {var subQ3=sQuery(id+"F0.wireOp",EDGE,"E1");var subQ9=sQuery(id+"F0.wireOp",EDGE,"E76.MirrorCS");var subQ11=makeQuery(id+"F0.imprint","INTERSECT",VERTEX,{"derivedFrom":[subQ3,subQ9]});Q49=makeQuery(id+"F0.imprint","IMPRINT",FACE,{"disambiguationData":[TD([[makeQuery(id+"F0.imprint","IMPRINT",EDGE,{"disambiguationData":[TD([[subQ11,-1.0]])],"derivedFrom":subQ3}),1.0]])]});}
            var Q50;
            {var subQ1=sQuery(id+"F0.wireOp",EDGE,"E72.MirrorCS");var subQ3=sQuery(id+"F0.wireOp",EDGE,"E1");var subQ4=makeQuery(id+"F0.imprint","INTERSECT",VERTEX,{"derivedFrom":[subQ3,subQ1]});Q50=makeQuery(id+"F0.imprint","IMPRINT",FACE,{"disambiguationData":[TD([[makeQuery(id+"F0.imprint","IMPRINT",EDGE,{"disambiguationData":[TD([[subQ4,-1.0]])],"derivedFrom":subQ3}),1.0]])]});}
            var Q51;
            {var subQ3=sQuery(id+"F0.wireOp",EDGE,"E1");var subQ6=sQuery(id+"F0.wireOp",EDGE,"E69.MirrorCS");var subQ8=makeQuery(id+"F0.imprint","INTERSECT",VERTEX,{"derivedFrom":[subQ3,subQ6]});Q51=makeQuery(id+"F0.imprint","IMPRINT",FACE,{"disambiguationData":[TD([[makeQuery(id+"F0.imprint","IMPRINT",EDGE,{"disambiguationData":[TD([[subQ8,-1.0]])],"derivedFrom":subQ3}),1.0]])]});}
            var Q52;
            {var subQ1=sQuery(id+"F0.wireOp",EDGE,"E70.MirrorCS");Q52=makeQuery(id+"F0.imprint","IMPRINT",FACE,{"disambiguationData":[TD([[makeQuery(id+"F0.imprint","IMPRINT",EDGE,{"derivedFrom":subQ1}),-1.0]])]});}
            var Q53;
            {var subQ1=sQuery(id+"F0.wireOp",EDGE,"E65.MirrorCS");var subQ5=sQuery(id+"F0.wireOp",EDGE,"E1");var subQ6=makeQuery(id+"F0.imprint","INTERSECT",VERTEX,{"derivedFrom":[subQ5,subQ1]});Q53=makeQuery(id+"F0.imprint","IMPRINT",FACE,{"disambiguationData":[TD([[makeQuery(id+"F0.imprint","IMPRINT",EDGE,{"disambiguationData":[TD([[subQ6,-1.0]])],"derivedFrom":subQ5}),1.0]])]});}
            var Q54;
            {var subQ0=sQuery(id+"F0.wireOp",EDGE,"E63.MirrorCS");Q54=makeQuery(id+"F0.imprint","IMPRINT",FACE,{"disambiguationData":[TD([[makeQuery(id+"F0.imprint","IMPRINT",EDGE,{"derivedFrom":subQ0}),-1.0]])]});}
            var Q55;
            {var subQ3=sQuery(id+"F0.wireOp",EDGE,"E1");var subQ9=sQuery(id+"F0.wireOp",EDGE,"E62.MirrorCS");var subQ11=makeQuery(id+"F0.imprint","INTERSECT",VERTEX,{"derivedFrom":[subQ3,subQ9]});Q55=makeQuery(id+"F0.imprint","IMPRINT",FACE,{"disambiguationData":[TD([[makeQuery(id+"F0.imprint","IMPRINT",EDGE,{"disambiguationData":[TD([[subQ11,-1.0]])],"derivedFrom":subQ3}),1.0]])]});}
            var Q56;
            {var subQ5=sQuery(id+"F0.wireOp",EDGE,"E58.MirrorCS");var subQ7=sQuery(id+"F0.wireOp",EDGE,"E1");var subQ8=makeQuery(id+"F0.imprint","INTERSECT",VERTEX,{"derivedFrom":[subQ7,subQ5]});Q56=makeQuery(id+"F0.imprint","IMPRINT",FACE,{"disambiguationData":[TD([[makeQuery(id+"F0.imprint","IMPRINT",EDGE,{"disambiguationData":[TD([[subQ8,-1.0]])],"derivedFrom":subQ7}),1.0]])]});}
            var Q57;
            {var subQ5=sQuery(id+"F0.wireOp",EDGE,"E1");var subQ8=sQuery(id+"F0.wireOp",EDGE,"E57.MirrorCS");var subQ10=makeQuery(id+"F0.imprint","INTERSECT",VERTEX,{"derivedFrom":[subQ5,subQ8]});Q57=makeQuery(id+"F0.imprint","IMPRINT",FACE,{"disambiguationData":[TD([[makeQuery(id+"F0.imprint","IMPRINT",EDGE,{"disambiguationData":[TD([[subQ10,-1.0]])],"derivedFrom":subQ5}),1.0]])]});}
            var Q58;
            {var subQ6=sQuery(id+"F0.wireOp",EDGE,"E55.MirrorCS");Q58=makeQuery(id+"F0.imprint","IMPRINT",FACE,{"disambiguationData":[TD([[makeQuery(id+"F0.imprint","IMPRINT",EDGE,{"derivedFrom":subQ6}),-1.0]])]});}
            var Q59;
            {var subQ1=sQuery(id+"F0.wireOp",EDGE,"E20");var subQ7=sQuery(id+"F0.wireOp",EDGE,"E1");var subQ8=makeQuery(id+"F0.imprint","INTERSECT",VERTEX,{"derivedFrom":[subQ7,subQ1]});Q59=makeQuery(id+"F0.imprint","IMPRINT",FACE,{"disambiguationData":[TD([[makeQuery(id+"F0.imprint","IMPRINT",EDGE,{"disambiguationData":[TD([[subQ8,-1.0]])],"derivedFrom":subQ7}),1.0]])]});}
            var Q60;
            Q60=makeQuery(id+"F0.imprint","IMPRINT",FACE,{"disambiguationData":[TD([[makeQuery(id+"F0.imprint","IMPRINT",EDGE,{"derivedFrom":sQuery(id+"F0.wireOp",EDGE,"E3")}),-1.0]])]});
            var Q61;
            {var subQ0=sQuery(id+"F0.wireOp",EDGE,"E169.MirrorCS");Q61=makeQuery(id+"F0.imprint","IMPRINT",FACE,{"disambiguationData":[TD([[makeQuery(id+"F0.imprint","IMPRINT",EDGE,{"derivedFrom":subQ0}),-1.0]])]});}
            var Q62;
            {var subQ0=sQuery(id+"F0.wireOp",EDGE,"E11");Q62=makeQuery(id+"F0.imprint","IMPRINT",FACE,{"disambiguationData":[TD([[makeQuery(id+"F0.imprint","IMPRINT",EDGE,{"derivedFrom":subQ0}),1.0]])]});}
            var Q63;
            {var subQ0=sQuery(id+"F0.wireOp",EDGE,"E47");Q63=makeQuery(id+"F0.imprint","IMPRINT",FACE,{"disambiguationData":[TD([[makeQuery(id+"F0.imprint","IMPRINT",EDGE,{"derivedFrom":subQ0}),1.0]])]});}
            var Q64;
            {var subQ0=sQuery(id+"F0.wireOp",EDGE,"E38");Q64=makeQuery(id+"F0.imprint","IMPRINT",FACE,{"disambiguationData":[TD([[makeQuery(id+"F0.imprint","IMPRINT",EDGE,{"derivedFrom":subQ0}),1.0]])]});}
            var Q65;
            {var subQ0=sQuery(id+"F0.wireOp",EDGE,"E30");Q65=makeQuery(id+"F0.imprint","IMPRINT",FACE,{"disambiguationData":[TD([[makeQuery(id+"F0.imprint","IMPRINT",EDGE,{"derivedFrom":subQ0}),1.0]])]});}
            var Q66;
            {var subQ0=sQuery(id+"F0.wireOp",EDGE,"E21");Q66=makeQuery(id+"F0.imprint","IMPRINT",FACE,{"disambiguationData":[TD([[makeQuery(id+"F0.imprint","IMPRINT",EDGE,{"derivedFrom":subQ0}),1.0]])]});}
            var Q67;
            {var subQ5=sQuery(id+"F0.wireOp",EDGE,"E1");var subQ6=makeQuery(id+"F0.imprint","INTERSECT",VERTEX,{"derivedFrom":[subQ5,sQuery(id+"F0.wireOp",EDGE,"E165.MirrorCS")]});Q67=makeQuery(id+"F0.imprint","IMPRINT",FACE,{"disambiguationData":[TD([[makeQuery(id+"F0.imprint","IMPRINT",EDGE,{"disambiguationData":[TD([[subQ6,1.0]])],"derivedFrom":subQ5}),1.0]])]});}
            var Q68;
            {var subQ0=sQuery(id+"F0.wireOp",EDGE,"E108.MirrorCS");var subQ5=sQuery(id+"F0.wireOp",EDGE,"E1");var subQ6=makeQuery(id+"F0.imprint","INTERSECT",VERTEX,{"derivedFrom":[subQ5,subQ0]});Q68=makeQuery(id+"F0.imprint","IMPRINT",FACE,{"disambiguationData":[TD([[makeQuery(id+"F0.imprint","IMPRINT",EDGE,{"disambiguationData":[TD([[subQ6,-1.0]])],"derivedFrom":subQ5}),1.0]])]});}
            var Q69;
            {var subQ5=sQuery(id+"F0.wireOp",EDGE,"E117.MirrorCS");Q69=makeQuery(id+"F0.imprint","IMPRINT",FACE,{"disambiguationData":[TD([[makeQuery(id+"F0.imprint","IMPRINT",EDGE,{"derivedFrom":subQ5}),1.0]])]});}
            extrude(context, id + "F1", {"entities" : qUnion([Q0, Q1, Q2, Q3, Q4, Q5, Q6, Q7, Q8, Q9, Q10, Q11, Q12, Q13, Q14, Q15, Q16, Q17, Q18, Q19, Q20, Q21, Q22, Q23, Q24, Q25, Q26, Q27, Q28, Q29, Q30, Q31, Q32, Q33, Q34, Q35, Q36, Q37, Q38, Q39, Q40, Q41, Q42, Q43, Q44, Q45, Q46, Q47, Q48, Q49, Q50, Q51, Q52, Q53, Q54, Q55, Q56, Q57, Q58, Q59, Q60, Q61, Q62, Q63, Q64, Q65, Q66, Q67, Q68, Q69]), "depth" : 6.35 * mm});
        }
        {
            var Q0;
            {var subQ4=sQuery(id+"F0.wireOp",EDGE,"E483.MirrorCS");Q0=makeQuery(id+"F0.imprint","IMPRINT",FACE,{"disambiguationData":[TD([[makeQuery(id+"F0.imprint","IMPRINT",EDGE,{"derivedFrom":subQ4}),-1.0]])]});}
            var Q1;
            {var subQ1=sQuery(id+"F0.wireOp",EDGE,"E484.MirrorCS");var subQ3=sQuery(id+"F0.wireOp",EDGE,"E0");var subQ4=makeQuery(id+"F0.imprint","INTERSECT",VERTEX,{"derivedFrom":[subQ3,subQ1]});Q1=makeQuery(id+"F0.imprint","IMPRINT",FACE,{"disambiguationData":[TD([[makeQuery(id+"F0.imprint","IMPRINT",EDGE,{"disambiguationData":[TD([[subQ4,-1.0]])],"derivedFrom":subQ3}),1.0]])]});}
            var Q2;
            {var subQ5=sQuery(id+"F0.wireOp",EDGE,"E326.MirrorCS");var subQ7=sQuery(id+"F0.wireOp",EDGE,"E0");var subQ8=makeQuery(id+"F0.imprint","INTERSECT",VERTEX,{"derivedFrom":[subQ7,subQ5]});Q2=makeQuery(id+"F0.imprint","IMPRINT",FACE,{"disambiguationData":[TD([[makeQuery(id+"F0.imprint","IMPRINT",EDGE,{"disambiguationData":[TD([[subQ8,1.0]])],"derivedFrom":subQ7}),1.0]])]});}
            var Q3;
            Q3=makeQuery(id+"F0.imprint","IMPRINT",FACE,{"disambiguationData":[TD([[makeQuery(id+"F0.imprint","IMPRINT",EDGE,{"derivedFrom":sQuery(id+"F0.wireOp",EDGE,"E2")}),-1.0]])]});
            var Q4;
            {var subQ6=sQuery(id+"F0.wireOp",EDGE,"E330.MirrorCS");var subQ9=sQuery(id+"F0.wireOp",EDGE,"E0");var subQ10=makeQuery(id+"F0.imprint","INTERSECT",VERTEX,{"derivedFrom":[subQ9,subQ6]});Q4=makeQuery(id+"F0.imprint","IMPRINT",FACE,{"disambiguationData":[TD([[makeQuery(id+"F0.imprint","IMPRINT",EDGE,{"disambiguationData":[TD([[subQ10,1.0]])],"derivedFrom":subQ9}),1.0]])]});}
            var Q5;
            {var subQ1=sQuery(id+"F0.wireOp",EDGE,"E327.MirrorCS");Q5=makeQuery(id+"F0.imprint","IMPRINT",FACE,{"disambiguationData":[TD([[makeQuery(id+"F0.imprint","IMPRINT",EDGE,{"derivedFrom":subQ1}),1.0]])]});}
            var Q6;
            {var subQ1=sQuery(id+"F0.wireOp",EDGE,"E479.MirrorCS");var subQ3=sQuery(id+"F0.wireOp",EDGE,"E0");var subQ4=makeQuery(id+"F0.imprint","INTERSECT",VERTEX,{"derivedFrom":[subQ3,subQ1]});Q6=makeQuery(id+"F0.imprint","IMPRINT",FACE,{"disambiguationData":[TD([[makeQuery(id+"F0.imprint","IMPRINT",EDGE,{"disambiguationData":[TD([[subQ4,-1.0]])],"derivedFrom":subQ3}),1.0]])]});}
            var Q7;
            {var subQ8=sQuery(id+"F0.wireOp",EDGE,"E0");var subQ12=makeQuery(id+"F0.imprint","INTERSECT",VERTEX,{"derivedFrom":[subQ8,sQuery(id+"F0.wireOp",EDGE,"E475.MirrorCS")]});Q7=makeQuery(id+"F0.imprint","IMPRINT",FACE,{"disambiguationData":[TD([[makeQuery(id+"F0.imprint","IMPRINT",EDGE,{"disambiguationData":[TD([[subQ12,1.0]])],"derivedFrom":subQ8}),1.0]])]});}
            var Q8;
            {var subQ0=sQuery(id+"F0.wireOp",EDGE,"E476.MirrorCS");Q8=makeQuery(id+"F0.imprint","IMPRINT",FACE,{"disambiguationData":[TD([[makeQuery(id+"F0.imprint","IMPRINT",EDGE,{"derivedFrom":subQ0}),-1.0]])]});}
            var Q9;
            {var subQ1=sQuery(id+"F0.wireOp",EDGE,"E330.MirrorCS");var subQ3=sQuery(id+"F0.wireOp",EDGE,"E0");var subQ4=makeQuery(id+"F0.imprint","INTERSECT",VERTEX,{"derivedFrom":[subQ3,subQ1]});Q9=makeQuery(id+"F0.imprint","IMPRINT",FACE,{"disambiguationData":[TD([[makeQuery(id+"F0.imprint","IMPRINT",EDGE,{"disambiguationData":[TD([[subQ4,-1.0]])],"derivedFrom":subQ3}),1.0]])]});}
            var Q10;
            {var subQ3=sQuery(id+"F0.wireOp",EDGE,"E0");var subQ5=makeQuery(id+"F0.imprint","INTERSECT",VERTEX,{"derivedFrom":[subQ3,sQuery(id+"F0.wireOp",EDGE,"E318.MirrorCS")]});Q10=makeQuery(id+"F0.imprint","IMPRINT",FACE,{"disambiguationData":[TD([[makeQuery(id+"F0.imprint","IMPRINT",EDGE,{"disambiguationData":[TD([[subQ5,1.0]])],"derivedFrom":subQ3}),1.0]])]});}
            var Q11;
            {var subQ0=sQuery(id+"F0.wireOp",EDGE,"E319.MirrorCS");Q11=makeQuery(id+"F0.imprint","IMPRINT",FACE,{"disambiguationData":[TD([[makeQuery(id+"F0.imprint","IMPRINT",EDGE,{"derivedFrom":subQ0}),1.0]])]});}
            var Q12;
            {var subQ1=sQuery(id+"F0.wireOp",EDGE,"E313.MirrorCS");var subQ3=sQuery(id+"F0.wireOp",EDGE,"E0");var subQ4=makeQuery(id+"F0.imprint","INTERSECT",VERTEX,{"derivedFrom":[subQ3,subQ1]});Q12=makeQuery(id+"F0.imprint","IMPRINT",FACE,{"disambiguationData":[TD([[makeQuery(id+"F0.imprint","IMPRINT",EDGE,{"disambiguationData":[TD([[subQ4,-1.0]])],"derivedFrom":subQ3}),1.0]])]});}
            var Q13;
            {var subQ1=sQuery(id+"F0.wireOp",EDGE,"E311.MirrorCS");Q13=makeQuery(id+"F0.imprint","IMPRINT",FACE,{"disambiguationData":[TD([[makeQuery(id+"F0.imprint","IMPRINT",EDGE,{"derivedFrom":subQ1}),1.0]])]});}
            var Q14;
            {var subQ1=sQuery(id+"F0.wireOp",EDGE,"E303.MirrorCS");Q14=makeQuery(id+"F0.imprint","IMPRINT",FACE,{"disambiguationData":[TD([[makeQuery(id+"F0.imprint","IMPRINT",EDGE,{"derivedFrom":subQ1}),1.0]])]});}
            var Q15;
            {var subQ1=sQuery(id+"F0.wireOp",EDGE,"E305.MirrorCS");var subQ8=sQuery(id+"F0.wireOp",EDGE,"E0");var subQ10=makeQuery(id+"F0.imprint","INTERSECT",VERTEX,{"derivedFrom":[subQ8,subQ1]});Q15=makeQuery(id+"F0.imprint","IMPRINT",FACE,{"disambiguationData":[TD([[makeQuery(id+"F0.imprint","IMPRINT",EDGE,{"disambiguationData":[TD([[subQ10,-1.0]])],"derivedFrom":subQ8}),1.0]])]});}
            var Q16;
            {var subQ0=sQuery(id+"F0.wireOp",EDGE,"E0");var subQ6=makeQuery(id+"F0.imprint","INTERSECT",VERTEX,{"derivedFrom":[subQ0,sQuery(id+"F0.wireOp",EDGE,"E297.MirrorCS")]});Q16=makeQuery(id+"F0.imprint","IMPRINT",FACE,{"disambiguationData":[TD([[makeQuery(id+"F0.imprint","IMPRINT",EDGE,{"disambiguationData":[TD([[subQ6,1.0]])],"derivedFrom":subQ0}),1.0]])]});}
            var Q17;
            {var subQ0=sQuery(id+"F0.wireOp",EDGE,"E295.MirrorCS");Q17=makeQuery(id+"F0.imprint","IMPRINT",FACE,{"disambiguationData":[TD([[makeQuery(id+"F0.imprint","IMPRINT",EDGE,{"derivedFrom":subQ0}),1.0]])]});}
            var Q18;
            {var subQ6=sQuery(id+"F0.wireOp",EDGE,"E287.MirrorCS");Q18=makeQuery(id+"F0.imprint","IMPRINT",FACE,{"disambiguationData":[TD([[makeQuery(id+"F0.imprint","IMPRINT",EDGE,{"derivedFrom":subQ6}),1.0]])]});}
            var Q19;
            {var subQ5=sQuery(id+"F0.wireOp",EDGE,"E0");var subQ6=makeQuery(id+"F0.imprint","INTERSECT",VERTEX,{"derivedFrom":[subQ5,sQuery(id+"F0.wireOp",EDGE,"E286.MirrorCS")]});Q19=makeQuery(id+"F0.imprint","IMPRINT",FACE,{"disambiguationData":[TD([[makeQuery(id+"F0.imprint","IMPRINT",EDGE,{"disambiguationData":[TD([[subQ6,1.0]])],"derivedFrom":subQ5}),1.0]])]});}
            var Q20;
            {var subQ1=sQuery(id+"F0.wireOp",EDGE,"E281.MirrorCS");var subQ3=sQuery(id+"F0.wireOp",EDGE,"E0");var subQ4=makeQuery(id+"F0.imprint","INTERSECT",VERTEX,{"derivedFrom":[subQ3,subQ1]});Q20=makeQuery(id+"F0.imprint","IMPRINT",FACE,{"disambiguationData":[TD([[makeQuery(id+"F0.imprint","IMPRINT",EDGE,{"disambiguationData":[TD([[subQ4,-1.0]])],"derivedFrom":subQ3}),1.0]])]});}
            var Q21;
            {var subQ1=sQuery(id+"F0.wireOp",EDGE,"E279.MirrorCS");Q21=makeQuery(id+"F0.imprint","IMPRINT",FACE,{"disambiguationData":[TD([[makeQuery(id+"F0.imprint","IMPRINT",EDGE,{"derivedFrom":subQ1}),1.0]])]});}
            var Q22;
            {var subQ1=sQuery(id+"F0.wireOp",EDGE,"E278.MirrorCS");var subQ3=sQuery(id+"F0.wireOp",EDGE,"E0");var subQ4=makeQuery(id+"F0.imprint","INTERSECT",VERTEX,{"derivedFrom":[subQ3,subQ1]});Q22=makeQuery(id+"F0.imprint","IMPRINT",FACE,{"disambiguationData":[TD([[makeQuery(id+"F0.imprint","IMPRINT",EDGE,{"disambiguationData":[TD([[subQ4,-1.0]])],"derivedFrom":subQ3}),1.0]])]});}
            var Q23;
            {var subQ6=sQuery(id+"F0.wireOp",EDGE,"E270.MirrorCS");Q23=makeQuery(id+"F0.imprint","IMPRINT",FACE,{"disambiguationData":[TD([[makeQuery(id+"F0.imprint","IMPRINT",EDGE,{"derivedFrom":subQ6}),1.0]])]});}
            var Q24;
            {var subQ5=sQuery(id+"F0.wireOp",EDGE,"E0");var subQ9=sQuery(id+"F0.wireOp",EDGE,"E272.MirrorCS");var subQ11=makeQuery(id+"F0.imprint","INTERSECT",VERTEX,{"derivedFrom":[subQ5,subQ9]});Q24=makeQuery(id+"F0.imprint","IMPRINT",FACE,{"disambiguationData":[TD([[makeQuery(id+"F0.imprint","IMPRINT",EDGE,{"disambiguationData":[TD([[subQ11,-1.0]])],"derivedFrom":subQ5}),1.0]])]});}
            var Q25;
            {var subQ0=sQuery(id+"F0.wireOp",EDGE,"E0");var subQ10=makeQuery(id+"F0.imprint","INTERSECT",VERTEX,{"derivedFrom":[subQ0,sQuery(id+"F0.wireOp",EDGE,"E264.MirrorCS")]});Q25=makeQuery(id+"F0.imprint","IMPRINT",FACE,{"disambiguationData":[TD([[makeQuery(id+"F0.imprint","IMPRINT",EDGE,{"disambiguationData":[TD([[subQ10,1.0]])],"derivedFrom":subQ0}),1.0]])]});}
            var Q26;
            {var subQ4=sQuery(id+"F0.wireOp",EDGE,"E262.MirrorCS");Q26=makeQuery(id+"F0.imprint","IMPRINT",FACE,{"disambiguationData":[TD([[makeQuery(id+"F0.imprint","IMPRINT",EDGE,{"derivedFrom":subQ4}),1.0]])]});}
            var Q27;
            Q27=makeQuery(id+"F0.imprint","IMPRINT",FACE,{"disambiguationData":[TD([[makeQuery(id+"F0.imprint","IMPRINT",EDGE,{"derivedFrom":sQuery(id+"F0.wireOp",EDGE,"E254.MirrorCS")}),1.0]])]});
            var Q28;
            {var subQ1=sQuery(id+"F0.wireOp",EDGE,"E199.MirrorCS");Q28=makeQuery(id+"F0.imprint","IMPRINT",FACE,{"disambiguationData":[TD([[makeQuery(id+"F0.imprint","IMPRINT",EDGE,{"derivedFrom":subQ1}),-1.0]])]});}
            var Q29;
            {var subQ1=sQuery(id+"F0.wireOp",EDGE,"E207.MirrorCS");Q29=makeQuery(id+"F0.imprint","IMPRINT",FACE,{"disambiguationData":[TD([[makeQuery(id+"F0.imprint","IMPRINT",EDGE,{"derivedFrom":subQ1}),-1.0]])]});}
            var Q30;
            {var subQ3=sQuery(id+"F0.wireOp",EDGE,"E0");var subQ6=sQuery(id+"F0.wireOp",EDGE,"E214.MirrorCS");var subQ10=makeQuery(id+"F0.imprint","INTERSECT",VERTEX,{"derivedFrom":[subQ3,subQ6]});Q30=makeQuery(id+"F0.imprint","IMPRINT",FACE,{"disambiguationData":[TD([[makeQuery(id+"F0.imprint","IMPRINT",EDGE,{"disambiguationData":[TD([[subQ10,-1.0]])],"derivedFrom":subQ3}),1.0]])]});}
            var Q31;
            {var subQ1=sQuery(id+"F0.wireOp",EDGE,"E215.MirrorCS");Q31=makeQuery(id+"F0.imprint","IMPRINT",FACE,{"disambiguationData":[TD([[makeQuery(id+"F0.imprint","IMPRINT",EDGE,{"derivedFrom":subQ1}),-1.0]])]});}
            var Q32;
            {var subQ3=sQuery(id+"F0.wireOp",EDGE,"E0");var subQ6=sQuery(id+"F0.wireOp",EDGE,"E217.MirrorCS");var subQ10=makeQuery(id+"F0.imprint","INTERSECT",VERTEX,{"derivedFrom":[subQ3,subQ6]});Q32=makeQuery(id+"F0.imprint","IMPRINT",FACE,{"disambiguationData":[TD([[makeQuery(id+"F0.imprint","IMPRINT",EDGE,{"disambiguationData":[TD([[subQ10,-1.0]])],"derivedFrom":subQ3}),1.0]])]});}
            var Q33;
            {var subQ1=sQuery(id+"F0.wireOp",EDGE,"E231.MirrorCS");Q33=makeQuery(id+"F0.imprint","IMPRINT",FACE,{"disambiguationData":[TD([[makeQuery(id+"F0.imprint","IMPRINT",EDGE,{"derivedFrom":subQ1}),-1.0]])]});}
            var Q34;
            {var subQ3=sQuery(id+"F0.wireOp",EDGE,"E0");var subQ6=sQuery(id+"F0.wireOp",EDGE,"E230.MirrorCS");var subQ10=makeQuery(id+"F0.imprint","INTERSECT",VERTEX,{"derivedFrom":[subQ3,subQ6]});Q34=makeQuery(id+"F0.imprint","IMPRINT",FACE,{"disambiguationData":[TD([[makeQuery(id+"F0.imprint","IMPRINT",EDGE,{"disambiguationData":[TD([[subQ10,-1.0]])],"derivedFrom":subQ3}),1.0]])]});}
            var Q35;
            {var subQ3=sQuery(id+"F0.wireOp",EDGE,"E0");var subQ5=makeQuery(id+"F0.imprint","INTERSECT",VERTEX,{"derivedFrom":[subQ3,sQuery(id+"F0.wireOp",EDGE,"E246.MirrorCS")]});Q35=makeQuery(id+"F0.imprint","IMPRINT",FACE,{"disambiguationData":[TD([[makeQuery(id+"F0.imprint","IMPRINT",EDGE,{"disambiguationData":[TD([[subQ5,1.0]])],"derivedFrom":subQ3}),1.0]])]});}
            var Q36;
            {var subQ1=sQuery(id+"F0.wireOp",EDGE,"E247.MirrorCS");Q36=makeQuery(id+"F0.imprint","IMPRINT",FACE,{"disambiguationData":[TD([[makeQuery(id+"F0.imprint","IMPRINT",EDGE,{"derivedFrom":subQ1}),-1.0]])]});}
            var Q37;
            {var subQ3=sQuery(id+"F0.wireOp",EDGE,"E0");var subQ6=makeQuery(id+"F0.imprint","INTERSECT",VERTEX,{"derivedFrom":[subQ3,sQuery(id+"F0.wireOp",EDGE,"E238.MirrorCS")]});Q37=makeQuery(id+"F0.imprint","IMPRINT",FACE,{"disambiguationData":[TD([[makeQuery(id+"F0.imprint","IMPRINT",EDGE,{"disambiguationData":[TD([[subQ6,1.0]])],"derivedFrom":subQ3}),1.0]])]});}
            var Q38;
            {var subQ1=sQuery(id+"F0.wireOp",EDGE,"E239.MirrorCS");Q38=makeQuery(id+"F0.imprint","IMPRINT",FACE,{"disambiguationData":[TD([[makeQuery(id+"F0.imprint","IMPRINT",EDGE,{"derivedFrom":subQ1}),-1.0]])]});}
            var Q39;
            {var subQ3=sQuery(id+"F0.wireOp",EDGE,"E0");var subQ5=sQuery(id+"F0.wireOp",EDGE,"E222.MirrorCS");var subQ6=makeQuery(id+"F0.imprint","INTERSECT",VERTEX,{"derivedFrom":[subQ3,subQ5]});Q39=makeQuery(id+"F0.imprint","IMPRINT",FACE,{"disambiguationData":[TD([[makeQuery(id+"F0.imprint","IMPRINT",EDGE,{"disambiguationData":[TD([[subQ6,-1.0]])],"derivedFrom":subQ3}),1.0]])]});}
            var Q40;
            {var subQ1=sQuery(id+"F0.wireOp",EDGE,"E223.MirrorCS");Q40=makeQuery(id+"F0.imprint","IMPRINT",FACE,{"disambiguationData":[TD([[makeQuery(id+"F0.imprint","IMPRINT",EDGE,{"derivedFrom":subQ1}),-1.0]])]});}
            var Q41;
            {var subQ1=sQuery(id+"F0.wireOp",EDGE,"E225.MirrorCS");var subQ3=sQuery(id+"F0.wireOp",EDGE,"E0");var subQ4=makeQuery(id+"F0.imprint","INTERSECT",VERTEX,{"derivedFrom":[subQ3,subQ1]});Q41=makeQuery(id+"F0.imprint","IMPRINT",FACE,{"disambiguationData":[TD([[makeQuery(id+"F0.imprint","IMPRINT",EDGE,{"disambiguationData":[TD([[subQ4,-1.0]])],"derivedFrom":subQ3}),1.0]])]});}
            var Q42;
            {var subQ3=sQuery(id+"F0.wireOp",EDGE,"E0");var subQ6=sQuery(id+"F0.wireOp",EDGE,"E190.MirrorCS");var subQ10=makeQuery(id+"F0.imprint","INTERSECT",VERTEX,{"derivedFrom":[subQ3,subQ6]});Q42=makeQuery(id+"F0.imprint","IMPRINT",FACE,{"disambiguationData":[TD([[makeQuery(id+"F0.imprint","IMPRINT",EDGE,{"disambiguationData":[TD([[subQ10,-1.0]])],"derivedFrom":subQ3}),1.0]])]});}
            var Q43;
            {var subQ1=sQuery(id+"F0.wireOp",EDGE,"E191.MirrorCS");Q43=makeQuery(id+"F0.imprint","IMPRINT",FACE,{"disambiguationData":[TD([[makeQuery(id+"F0.imprint","IMPRINT",EDGE,{"derivedFrom":subQ1}),-1.0]])]});}
            var Q44;
            {var subQ1=sQuery(id+"F0.wireOp",EDGE,"E183.MirrorCS");Q44=makeQuery(id+"F0.imprint","IMPRINT",FACE,{"disambiguationData":[TD([[makeQuery(id+"F0.imprint","IMPRINT",EDGE,{"derivedFrom":subQ1}),-1.0]])]});}
            var Q45;
            {var subQ5=sQuery(id+"F0.wireOp",EDGE,"E0");var subQ6=makeQuery(id+"F0.imprint","INTERSECT",VERTEX,{"derivedFrom":[subQ5,sQuery(id+"F0.wireOp",EDGE,"E182.MirrorCS")]});Q45=makeQuery(id+"F0.imprint","IMPRINT",FACE,{"disambiguationData":[TD([[makeQuery(id+"F0.imprint","IMPRINT",EDGE,{"disambiguationData":[TD([[subQ6,1.0]])],"derivedFrom":subQ5}),1.0]])]});}
            var Q46;
            {var subQ1=sQuery(id+"F0.wireOp",EDGE,"E185.MirrorCS");var subQ3=sQuery(id+"F0.wireOp",EDGE,"E0");var subQ4=makeQuery(id+"F0.imprint","INTERSECT",VERTEX,{"derivedFrom":[subQ3,subQ1]});Q46=makeQuery(id+"F0.imprint","IMPRINT",FACE,{"disambiguationData":[TD([[makeQuery(id+"F0.imprint","IMPRINT",EDGE,{"disambiguationData":[TD([[subQ4,-1.0]])],"derivedFrom":subQ3}),1.0]])]});}
            var Q47;
            {var subQ3=sQuery(id+"F0.wireOp",EDGE,"E0");var subQ6=sQuery(id+"F0.wireOp",EDGE,"E174.MirrorCS");var subQ10=makeQuery(id+"F0.imprint","INTERSECT",VERTEX,{"derivedFrom":[subQ3,subQ6]});Q47=makeQuery(id+"F0.imprint","IMPRINT",FACE,{"disambiguationData":[TD([[makeQuery(id+"F0.imprint","IMPRINT",EDGE,{"disambiguationData":[TD([[subQ10,-1.0]])],"derivedFrom":subQ3}),1.0]])]});}
            var Q48;
            {var subQ1=sQuery(id+"F0.wireOp",EDGE,"E175.MirrorCS");Q48=makeQuery(id+"F0.imprint","IMPRINT",FACE,{"disambiguationData":[TD([[makeQuery(id+"F0.imprint","IMPRINT",EDGE,{"derivedFrom":subQ1}),-1.0]])]});}
            var Q49;
            {var subQ3=sQuery(id+"F0.wireOp",EDGE,"E0");var subQ6=sQuery(id+"F0.wireOp",EDGE,"E177.MirrorCS");var subQ8=makeQuery(id+"F0.imprint","INTERSECT",VERTEX,{"derivedFrom":[subQ3,subQ6]});Q49=makeQuery(id+"F0.imprint","IMPRINT",FACE,{"disambiguationData":[TD([[makeQuery(id+"F0.imprint","IMPRINT",EDGE,{"disambiguationData":[TD([[subQ8,-1.0]])],"derivedFrom":subQ3}),1.0]])]});}
            var Q50;
            {var subQ1=sQuery(id+"F0.wireOp",EDGE,"E338.MirrorCS");var subQ5=sQuery(id+"F0.wireOp",EDGE,"E0");var subQ6=makeQuery(id+"F0.imprint","INTERSECT",VERTEX,{"derivedFrom":[subQ5,subQ1]});Q50=makeQuery(id+"F0.imprint","IMPRINT",FACE,{"disambiguationData":[TD([[makeQuery(id+"F0.imprint","IMPRINT",EDGE,{"disambiguationData":[TD([[subQ6,-1.0]])],"derivedFrom":subQ5}),1.0]])]});}
            var Q51;
            {var subQ0=sQuery(id+"F0.wireOp",EDGE,"E335.MirrorCS");Q51=makeQuery(id+"F0.imprint","IMPRINT",FACE,{"disambiguationData":[TD([[makeQuery(id+"F0.imprint","IMPRINT",EDGE,{"derivedFrom":subQ0}),1.0]])]});}
            var Q52;
            {var subQ3=sQuery(id+"F0.wireOp",EDGE,"E0");var subQ6=sQuery(id+"F0.wireOp",EDGE,"E334.MirrorCS");var subQ10=makeQuery(id+"F0.imprint","INTERSECT",VERTEX,{"derivedFrom":[subQ3,subQ6]});Q52=makeQuery(id+"F0.imprint","IMPRINT",FACE,{"disambiguationData":[TD([[makeQuery(id+"F0.imprint","IMPRINT",EDGE,{"disambiguationData":[TD([[subQ10,-1.0]])],"derivedFrom":subQ3}),1.0]])]});}
            var Q53;
            {var subQ5=sQuery(id+"F0.wireOp",EDGE,"E0");var subQ9=makeQuery(id+"F0.imprint","INTERSECT",VERTEX,{"derivedFrom":[subQ5,sQuery(id+"F0.wireOp",EDGE,"E342.MirrorCS")]});Q53=makeQuery(id+"F0.imprint","IMPRINT",FACE,{"disambiguationData":[TD([[makeQuery(id+"F0.imprint","IMPRINT",EDGE,{"disambiguationData":[TD([[subQ9,1.0]])],"derivedFrom":subQ5}),1.0]])]});}
            var Q54;
            {var subQ1=sQuery(id+"F0.wireOp",EDGE,"E343.MirrorCS");Q54=makeQuery(id+"F0.imprint","IMPRINT",FACE,{"disambiguationData":[TD([[makeQuery(id+"F0.imprint","IMPRINT",EDGE,{"derivedFrom":subQ1}),1.0]])]});}
            var Q55;
            {var subQ0=sQuery(id+"F0.wireOp",EDGE,"E351.MirrorCS");var subQ3=sQuery(id+"F0.wireOp",EDGE,"E0");var subQ4=makeQuery(id+"F0.imprint","INTERSECT",VERTEX,{"derivedFrom":[subQ3,subQ0]});Q55=makeQuery(id+"F0.imprint","IMPRINT",FACE,{"disambiguationData":[TD([[makeQuery(id+"F0.imprint","IMPRINT",EDGE,{"disambiguationData":[TD([[subQ4,-1.0]])],"derivedFrom":subQ3}),1.0]])]});}
            var Q56;
            {var subQ0=sQuery(id+"F0.wireOp",EDGE,"E354.MirrorCS");Q56=makeQuery(id+"F0.imprint","IMPRINT",FACE,{"disambiguationData":[TD([[makeQuery(id+"F0.imprint","IMPRINT",EDGE,{"derivedFrom":subQ0}),1.0]])]});}
            var Q57;
            {var subQ0=sQuery(id+"F0.wireOp",EDGE,"E353.MirrorCS");var subQ3=sQuery(id+"F0.wireOp",EDGE,"E0");var subQ4=makeQuery(id+"F0.imprint","INTERSECT",VERTEX,{"derivedFrom":[subQ3,subQ0]});Q57=makeQuery(id+"F0.imprint","IMPRINT",FACE,{"disambiguationData":[TD([[makeQuery(id+"F0.imprint","IMPRINT",EDGE,{"disambiguationData":[TD([[subQ4,-1.0]])],"derivedFrom":subQ3}),1.0]])]});}
            var Q58;
            {var subQ1=sQuery(id+"F0.wireOp",EDGE,"E364.MirrorCS");var subQ3=sQuery(id+"F0.wireOp",EDGE,"E0");var subQ4=makeQuery(id+"F0.imprint","INTERSECT",VERTEX,{"derivedFrom":[subQ3,subQ1]});Q58=makeQuery(id+"F0.imprint","IMPRINT",FACE,{"disambiguationData":[TD([[makeQuery(id+"F0.imprint","IMPRINT",EDGE,{"disambiguationData":[TD([[subQ4,-1.0]])],"derivedFrom":subQ3}),1.0]])]});}
            var Q59;
            {var subQ0=sQuery(id+"F0.wireOp",EDGE,"E361.MirrorCS");Q59=makeQuery(id+"F0.imprint","IMPRINT",FACE,{"disambiguationData":[TD([[makeQuery(id+"F0.imprint","IMPRINT",EDGE,{"derivedFrom":subQ0}),1.0]])]});}
            var Q60;
            {var subQ5=sQuery(id+"F0.wireOp",EDGE,"E0");var subQ9=makeQuery(id+"F0.imprint","INTERSECT",VERTEX,{"derivedFrom":[subQ5,sQuery(id+"F0.wireOp",EDGE,"E369.MirrorCS")]});Q60=makeQuery(id+"F0.imprint","IMPRINT",FACE,{"disambiguationData":[TD([[makeQuery(id+"F0.imprint","IMPRINT",EDGE,{"disambiguationData":[TD([[subQ9,1.0]])],"derivedFrom":subQ5}),1.0]])]});}
            var Q61;
            {var subQ1=sQuery(id+"F0.wireOp",EDGE,"E367.MirrorCS");Q61=makeQuery(id+"F0.imprint","IMPRINT",FACE,{"disambiguationData":[TD([[makeQuery(id+"F0.imprint","IMPRINT",EDGE,{"derivedFrom":subQ1}),1.0]])]});}
            var Q62;
            {var subQ5=sQuery(id+"F0.wireOp",EDGE,"E0");var subQ6=makeQuery(id+"F0.imprint","INTERSECT",VERTEX,{"derivedFrom":[subQ5,sQuery(id+"F0.wireOp",EDGE,"E377.MirrorCS")]});Q62=makeQuery(id+"F0.imprint","IMPRINT",FACE,{"disambiguationData":[TD([[makeQuery(id+"F0.imprint","IMPRINT",EDGE,{"disambiguationData":[TD([[subQ6,1.0]])],"derivedFrom":subQ5}),1.0]])]});}
            var Q63;
            {var subQ0=sQuery(id+"F0.wireOp",EDGE,"E379.MirrorCS");Q63=makeQuery(id+"F0.imprint","IMPRINT",FACE,{"disambiguationData":[TD([[makeQuery(id+"F0.imprint","IMPRINT",EDGE,{"derivedFrom":subQ0}),1.0]])]});}
            var Q64;
            {var subQ0=sQuery(id+"F0.wireOp",EDGE,"E383.MirrorCS");var subQ3=sQuery(id+"F0.wireOp",EDGE,"E0");var subQ4=makeQuery(id+"F0.imprint","INTERSECT",VERTEX,{"derivedFrom":[subQ3,subQ0]});Q64=makeQuery(id+"F0.imprint","IMPRINT",FACE,{"disambiguationData":[TD([[makeQuery(id+"F0.imprint","IMPRINT",EDGE,{"disambiguationData":[TD([[subQ4,-1.0]])],"derivedFrom":subQ3}),1.0]])]});}
            var Q65;
            {var subQ0=sQuery(id+"F0.wireOp",EDGE,"E387.MirrorCS");Q65=makeQuery(id+"F0.imprint","IMPRINT",FACE,{"disambiguationData":[TD([[makeQuery(id+"F0.imprint","IMPRINT",EDGE,{"derivedFrom":subQ0}),1.0]])]});}
            var Q66;
            {var subQ1=sQuery(id+"F0.wireOp",EDGE,"E384.MirrorCS");var subQ5=sQuery(id+"F0.wireOp",EDGE,"E0");var subQ6=makeQuery(id+"F0.imprint","INTERSECT",VERTEX,{"derivedFrom":[subQ5,subQ1]});Q66=makeQuery(id+"F0.imprint","IMPRINT",FACE,{"disambiguationData":[TD([[makeQuery(id+"F0.imprint","IMPRINT",EDGE,{"disambiguationData":[TD([[subQ6,-1.0]])],"derivedFrom":subQ5}),1.0]])]});}
            var Q67;
            {var subQ0=sQuery(id+"F0.wireOp",EDGE,"E392.MirrorCS");var subQ3=sQuery(id+"F0.wireOp",EDGE,"E0");var subQ4=makeQuery(id+"F0.imprint","INTERSECT",VERTEX,{"derivedFrom":[subQ3,subQ0]});Q67=makeQuery(id+"F0.imprint","IMPRINT",FACE,{"disambiguationData":[TD([[makeQuery(id+"F0.imprint","IMPRINT",EDGE,{"disambiguationData":[TD([[subQ4,-1.0]])],"derivedFrom":subQ3}),1.0]])]});}
            var Q68;
            {var subQ0=sQuery(id+"F0.wireOp",EDGE,"E395.MirrorCS");Q68=makeQuery(id+"F0.imprint","IMPRINT",FACE,{"disambiguationData":[TD([[makeQuery(id+"F0.imprint","IMPRINT",EDGE,{"derivedFrom":subQ0}),1.0]])]});}
            var Q69;
            {var subQ0=sQuery(id+"F0.wireOp",EDGE,"E0");var subQ16=makeQuery(id+"F0.imprint","INTERSECT",VERTEX,{"derivedFrom":[subQ0,sQuery(id+"F0.wireOp",EDGE,"E399.MirrorCS")]});Q69=makeQuery(id+"F0.imprint","IMPRINT",FACE,{"disambiguationData":[TD([[makeQuery(id+"F0.imprint","IMPRINT",EDGE,{"disambiguationData":[TD([[subQ16,1.0]])],"derivedFrom":subQ0}),1.0]])]});}
            var Q70;
            {var subQ0=sQuery(id+"F0.wireOp",EDGE,"E403.MirrorCS");Q70=makeQuery(id+"F0.imprint","IMPRINT",FACE,{"disambiguationData":[TD([[makeQuery(id+"F0.imprint","IMPRINT",EDGE,{"derivedFrom":subQ0}),1.0]])]});}
            var Q71;
            {var subQ0=sQuery(id+"F0.wireOp",EDGE,"E410.MirrorCS");Q71=makeQuery(id+"F0.imprint","IMPRINT",FACE,{"disambiguationData":[TD([[makeQuery(id+"F0.imprint","IMPRINT",EDGE,{"derivedFrom":subQ0}),1.0]])]});}
            var Q72;
            {var subQ0=sQuery(id+"F0.wireOp",EDGE,"E418.MirrorCS");Q72=makeQuery(id+"F0.imprint","IMPRINT",FACE,{"disambiguationData":[TD([[makeQuery(id+"F0.imprint","IMPRINT",EDGE,{"derivedFrom":subQ0}),-1.0]])]});}
            var Q73;
            {var subQ4=sQuery(id+"F0.wireOp",EDGE,"E426.MirrorCS");Q73=makeQuery(id+"F0.imprint","IMPRINT",FACE,{"disambiguationData":[TD([[makeQuery(id+"F0.imprint","IMPRINT",EDGE,{"derivedFrom":subQ4}),-1.0]])]});}
            var Q74;
            {var subQ0=sQuery(id+"F0.wireOp",EDGE,"E433.MirrorCS");Q74=makeQuery(id+"F0.imprint","IMPRINT",FACE,{"disambiguationData":[TD([[makeQuery(id+"F0.imprint","IMPRINT",EDGE,{"derivedFrom":subQ0}),-1.0]])]});}
            var Q75;
            {var subQ6=sQuery(id+"F0.wireOp",EDGE,"E429.MirrorCS");var subQ8=sQuery(id+"F0.wireOp",EDGE,"E0");var subQ9=makeQuery(id+"F0.imprint","INTERSECT",VERTEX,{"derivedFrom":[subQ8,subQ6]});Q75=makeQuery(id+"F0.imprint","IMPRINT",FACE,{"disambiguationData":[TD([[makeQuery(id+"F0.imprint","IMPRINT",EDGE,{"disambiguationData":[TD([[subQ9,-1.0]])],"derivedFrom":subQ8}),1.0]])]});}
            var Q76;
            {var subQ1=sQuery(id+"F0.wireOp",EDGE,"E436.MirrorCS");var subQ3=sQuery(id+"F0.wireOp",EDGE,"E0");var subQ4=makeQuery(id+"F0.imprint","INTERSECT",VERTEX,{"derivedFrom":[subQ3,subQ1]});Q76=makeQuery(id+"F0.imprint","IMPRINT",FACE,{"disambiguationData":[TD([[makeQuery(id+"F0.imprint","IMPRINT",EDGE,{"disambiguationData":[TD([[subQ4,-1.0]])],"derivedFrom":subQ3}),1.0]])]});}
            var Q77;
            {var subQ0=sQuery(id+"F0.wireOp",EDGE,"E437.MirrorCS");Q77=makeQuery(id+"F0.imprint","IMPRINT",FACE,{"disambiguationData":[TD([[makeQuery(id+"F0.imprint","IMPRINT",EDGE,{"derivedFrom":subQ0}),-1.0]])]});}
            var Q78;
            {var subQ1=sQuery(id+"F0.wireOp",EDGE,"E444.MirrorCS");Q78=makeQuery(id+"F0.imprint","IMPRINT",FACE,{"disambiguationData":[TD([[makeQuery(id+"F0.imprint","IMPRINT",EDGE,{"derivedFrom":subQ1}),-1.0]])]});}
            var Q79;
            {var subQ3=sQuery(id+"F0.wireOp",EDGE,"E0");var subQ9=makeQuery(id+"F0.imprint","INTERSECT",VERTEX,{"derivedFrom":[subQ3,sQuery(id+"F0.wireOp",EDGE,"E446.MirrorCS")]});Q79=makeQuery(id+"F0.imprint","IMPRINT",FACE,{"disambiguationData":[TD([[makeQuery(id+"F0.imprint","IMPRINT",EDGE,{"disambiguationData":[TD([[subQ9,1.0]])],"derivedFrom":subQ3}),1.0]])]});}
            var Q80;
            {var subQ1=sQuery(id+"F0.wireOp",EDGE,"E451.MirrorCS");Q80=makeQuery(id+"F0.imprint","IMPRINT",FACE,{"disambiguationData":[TD([[makeQuery(id+"F0.imprint","IMPRINT",EDGE,{"derivedFrom":subQ1}),-1.0]])]});}
            var Q81;
            {var subQ7=sQuery(id+"F0.wireOp",EDGE,"E0");var subQ10=makeQuery(id+"F0.imprint","INTERSECT",VERTEX,{"derivedFrom":[subQ7,sQuery(id+"F0.wireOp",EDGE,"E454.MirrorCS")]});Q81=makeQuery(id+"F0.imprint","IMPRINT",FACE,{"disambiguationData":[TD([[makeQuery(id+"F0.imprint","IMPRINT",EDGE,{"disambiguationData":[TD([[subQ10,1.0]])],"derivedFrom":subQ7}),1.0]])]});}
            var Q82;
            {var subQ3=sQuery(id+"F0.wireOp",EDGE,"E0");var subQ9=sQuery(id+"F0.wireOp",EDGE,"E459.MirrorCS");var subQ11=makeQuery(id+"F0.imprint","INTERSECT",VERTEX,{"derivedFrom":[subQ3,subQ9]});Q82=makeQuery(id+"F0.imprint","IMPRINT",FACE,{"disambiguationData":[TD([[makeQuery(id+"F0.imprint","IMPRINT",EDGE,{"disambiguationData":[TD([[subQ11,-1.0]])],"derivedFrom":subQ3}),1.0]])]});}
            var Q83;
            {var subQ1=sQuery(id+"F0.wireOp",EDGE,"E460.MirrorCS");Q83=makeQuery(id+"F0.imprint","IMPRINT",FACE,{"disambiguationData":[TD([[makeQuery(id+"F0.imprint","IMPRINT",EDGE,{"derivedFrom":subQ1}),-1.0]])]});}
            var Q84;
            {var subQ0=sQuery(id+"F0.wireOp",EDGE,"E472.MirrorCS");Q84=makeQuery(id+"F0.imprint","IMPRINT",FACE,{"disambiguationData":[TD([[makeQuery(id+"F0.imprint","IMPRINT",EDGE,{"derivedFrom":subQ0}),-1.0]])]});}
            var Q85;
            {var subQ1=sQuery(id+"F0.wireOp",EDGE,"E467.MirrorCS");var subQ3=sQuery(id+"F0.wireOp",EDGE,"E0");var subQ4=makeQuery(id+"F0.imprint","INTERSECT",VERTEX,{"derivedFrom":[subQ3,subQ1]});Q85=makeQuery(id+"F0.imprint","IMPRINT",FACE,{"disambiguationData":[TD([[makeQuery(id+"F0.imprint","IMPRINT",EDGE,{"disambiguationData":[TD([[subQ4,-1.0]])],"derivedFrom":subQ3}),1.0]])]});}
            var Q86;
            {var subQ1=sQuery(id+"F0.wireOp",EDGE,"E463.MirrorCS");var subQ7=sQuery(id+"F0.wireOp",EDGE,"E0");var subQ8=makeQuery(id+"F0.imprint","INTERSECT",VERTEX,{"derivedFrom":[subQ7,subQ1]});Q86=makeQuery(id+"F0.imprint","IMPRINT",FACE,{"disambiguationData":[TD([[makeQuery(id+"F0.imprint","IMPRINT",EDGE,{"disambiguationData":[TD([[subQ8,-1.0]])],"derivedFrom":subQ7}),1.0]])]});}
            var Q87;
            {var subQ6=sQuery(id+"F0.wireOp",EDGE,"E310.MirrorCS");var subQ8=sQuery(id+"F0.wireOp",EDGE,"E0");var subQ9=makeQuery(id+"F0.imprint","INTERSECT",VERTEX,{"derivedFrom":[subQ8,subQ6]});Q87=makeQuery(id+"F0.imprint","IMPRINT",FACE,{"disambiguationData":[TD([[makeQuery(id+"F0.imprint","IMPRINT",EDGE,{"disambiguationData":[TD([[subQ9,-1.0]])],"derivedFrom":subQ8}),1.0]])]});}
            var Q88;
            {var subQ0=sQuery(id+"F0.wireOp",EDGE,"E432.MirrorCS");var subQ5=sQuery(id+"F0.wireOp",EDGE,"E0");var subQ6=makeQuery(id+"F0.imprint","INTERSECT",VERTEX,{"derivedFrom":[subQ5,subQ0]});Q88=makeQuery(id+"F0.imprint","IMPRINT",FACE,{"disambiguationData":[TD([[makeQuery(id+"F0.imprint","IMPRINT",EDGE,{"disambiguationData":[TD([[subQ6,-1.0]])],"derivedFrom":subQ5}),1.0]])]});}
            var Q89;
            {var subQ1=sQuery(id+"F0.wireOp",EDGE,"E209.MirrorCS");var subQ8=sQuery(id+"F0.wireOp",EDGE,"E0");var subQ10=makeQuery(id+"F0.imprint","INTERSECT",VERTEX,{"derivedFrom":[subQ8,subQ1]});Q89=makeQuery(id+"F0.imprint","IMPRINT",FACE,{"disambiguationData":[TD([[makeQuery(id+"F0.imprint","IMPRINT",EDGE,{"disambiguationData":[TD([[subQ10,-1.0]])],"derivedFrom":subQ8}),1.0]])]});}
            var Q90;
            {var subQ3=sQuery(id+"F0.wireOp",EDGE,"E0");var subQ6=sQuery(id+"F0.wireOp",EDGE,"E206.MirrorCS");var subQ10=makeQuery(id+"F0.imprint","INTERSECT",VERTEX,{"derivedFrom":[subQ3,subQ6]});Q90=makeQuery(id+"F0.imprint","IMPRINT",FACE,{"disambiguationData":[TD([[makeQuery(id+"F0.imprint","IMPRINT",EDGE,{"disambiguationData":[TD([[subQ10,-1.0]])],"derivedFrom":subQ3}),1.0]])]});}
            extrude(context, id + "F2", {"entities" : qUnion([Q0, Q1, Q2, Q3, Q4, Q5, Q6, Q7, Q8, Q9, Q10, Q11, Q12, Q13, Q14, Q15, Q16, Q17, Q18, Q19, Q20, Q21, Q22, Q23, Q24, Q25, Q26, Q27, Q28, Q29, Q30, Q31, Q32, Q33, Q34, Q35, Q36, Q37, Q38, Q39, Q40, Q41, Q42, Q43, Q44, Q45, Q46, Q47, Q48, Q49, Q50, Q51, Q52, Q53, Q54, Q55, Q56, Q57, Q58, Q59, Q60, Q61, Q62, Q63, Q64, Q65, Q66, Q67, Q68, Q69, Q70, Q71, Q72, Q73, Q74, Q75, Q76, Q77, Q78, Q79, Q80, Q81, Q82, Q83, Q84, Q85, Q86, Q87, Q88, Q89, Q90]), "depth" : 12.7 * mm});
        }
    });
